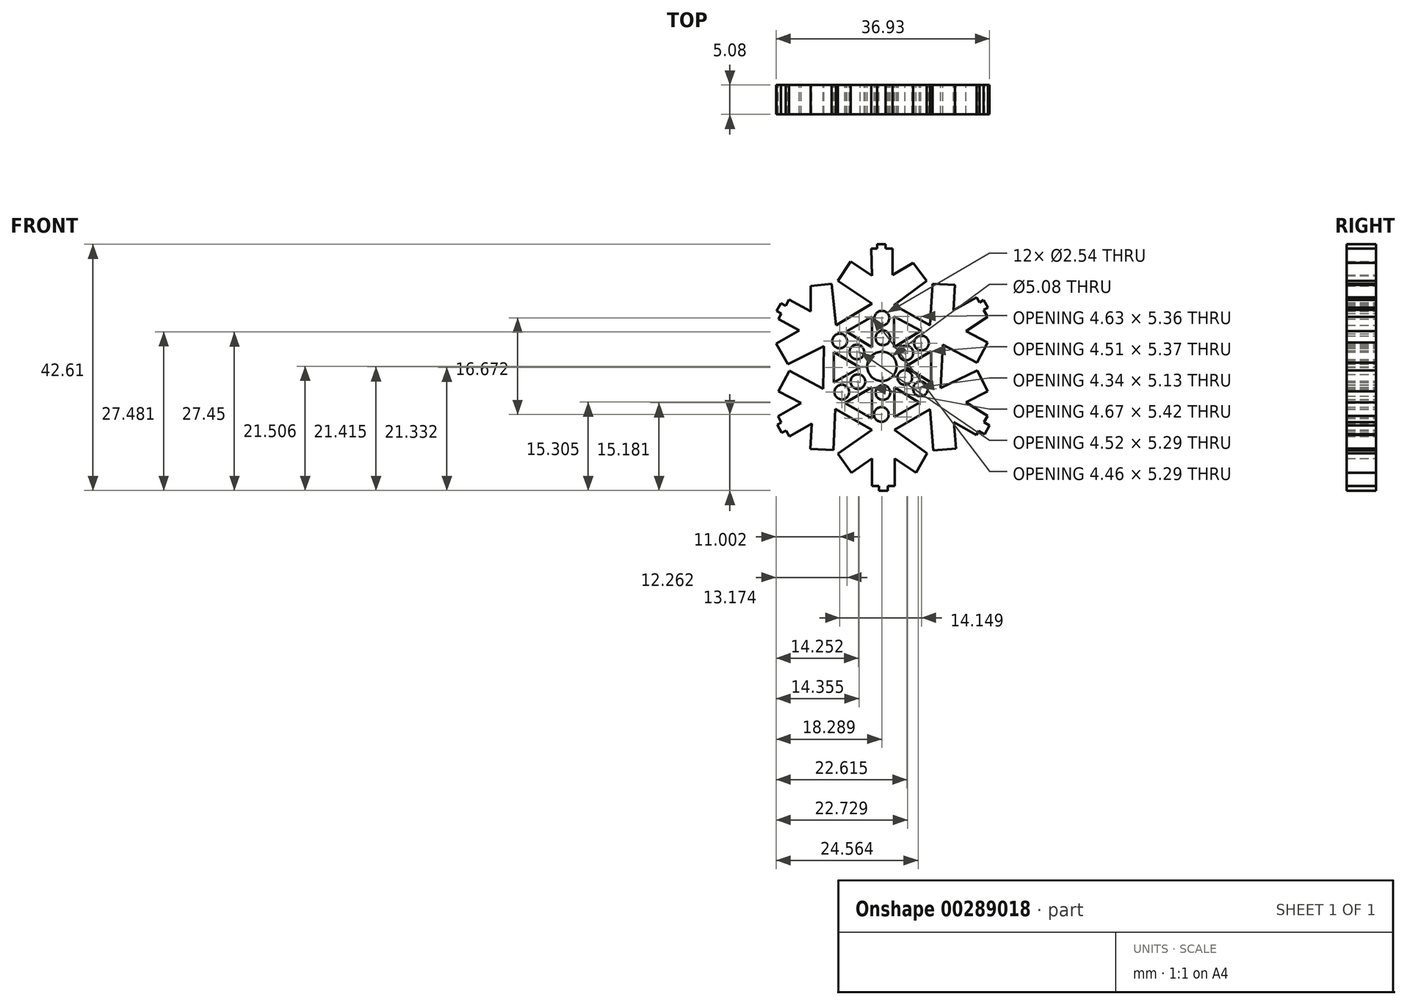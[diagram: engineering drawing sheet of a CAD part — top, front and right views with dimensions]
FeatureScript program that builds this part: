
annotation { "Feature Type Name" : "Feature", "Feature Type Description" : "" }
export const myFeature = defineFeature(function(context is Context, id is Id, definition is map)
    precondition{}
    {
        {
            var Q0;
            Q0=qCreatedBy(makeId("Front.planeOp"),FACE);
            var sketch = newSketch(context, id + "F0", { "sketchPlane" : qUnion([Q0])});
            skLineSegment(sketch, "E0", {"start": v(-24.04, 42.31) * mm, "end": v(-20.36, 42.31) * mm});
            skLineSegment(sketch, "E1", {"start": v(-20.36, 42.31) * mm, "end": v(-20.36, 37.78) * mm});
            skLineSegment(sketch, "E2", {"start": v(-20.36, 37.78) * mm, "end": v(-16.78, 39.86) * mm});
            skLineSegment(sketch, "E3", {"start": v(-16.78, 39.86) * mm, "end": v(-14.46, 36.74) * mm});
            skLineSegment(sketch, "E4", {"start": v(-14.46, 36.74) * mm, "end": v(-20.09, 32.57) * mm});
            skLineSegment(sketch, "E5", {"start": v(-20.09, 32.57) * mm, "end": v(-20.09, 25.26) * mm});
            skLineSegment(sketch, "E6", {"start": v(-20.09, 25.26) * mm, "end": v(-13.89, 29.04) * mm});
            skLineSegment(sketch, "E7", {"start": v(-13.89, 29.04) * mm, "end": v(-13.46, 36.26) * mm});
            skLineSegment(sketch, "E8", {"start": v(-13.46, 36.26) * mm, "end": v(-9.57, 36.03) * mm});
            skLineSegment(sketch, "E9", {"start": v(-9.57, 36.03) * mm, "end": v(-9.83, 31.68) * mm});
            skLineSegment(sketch, "E10", {"start": v(-9.83, 31.68) * mm, "end": v(-5.8, 33.92) * mm});
            skLineSegment(sketch, "E11", {"start": v(-5.8, 33.92) * mm, "end": v(-3.94, 30.55) * mm});
            skLineSegment(sketch, "E12", {"start": v(-3.94, 30.55) * mm, "end": v(-7.67, 28.04) * mm});
            skLineSegment(sketch, "E13", {"start": v(-7.67, 28.04) * mm, "end": v(-3.94, 26.08) * mm});
            skLineSegment(sketch, "E14", {"start": v(-3.94, 26.08) * mm, "end": v(-5.76, 22.61) * mm});
            skLineSegment(sketch, "E15", {"start": v(-5.76, 22.61) * mm, "end": v(-11.69, 25.73) * mm});
            skLineSegment(sketch, "E16", {"start": v(-11.69, 25.73) * mm, "end": v(-18.2, 21.92) * mm});
            skLineSegment(sketch, "E17", {"start": v(-18.2, 21.92) * mm, "end": v(-12.02, 18.19) * mm});
            skLineSegment(sketch, "E18", {"start": v(-12.02, 18.19) * mm, "end": v(-5.67, 21.25) * mm});
            skLineSegment(sketch, "E19", {"start": v(-5.67, 21.25) * mm, "end": v(-3.94, 17.66) * mm});
            skLineSegment(sketch, "E20", {"start": v(-3.94, 17.66) * mm, "end": v(-7.67, 15.75) * mm});
            skLineSegment(sketch, "E21", {"start": v(-7.67, 15.75) * mm, "end": v(-3.94, 13.38) * mm});
            skLineSegment(sketch, "E22", {"start": v(-3.94, 13.38) * mm, "end": v(-5.85, 10.05) * mm});
            skLineSegment(sketch, "E23", {"start": v(-5.85, 10.05) * mm, "end": v(-9.73, 12.28) * mm});
            skLineSegment(sketch, "E24", {"start": v(-9.73, 12.28) * mm, "end": v(-9.37, 7.74) * mm});
            skLineSegment(sketch, "E25", {"start": v(-9.37, 7.74) * mm, "end": v(-13.3, 7.43) * mm});
            skLineSegment(sketch, "E26", {"start": v(-13.3, 7.43) * mm, "end": v(-13.86, 14.5) * mm});
            skLineSegment(sketch, "E27", {"start": v(-13.86, 14.5) * mm, "end": v(-20.03, 18.33) * mm});
            skLineSegment(sketch, "E28", {"start": v(-20.03, 18.33) * mm, "end": v(-20.07, 11) * mm});
            skLineSegment(sketch, "E29", {"start": v(-20.07, 11) * mm, "end": v(-14.36, 6.91) * mm});
            skLineSegment(sketch, "E30", {"start": v(-14.36, 6.91) * mm, "end": v(-16.32, 3.55) * mm});
            skLineSegment(sketch, "E31", {"start": v(-16.32, 3.55) * mm, "end": v(-19.95, 6.04) * mm});
            skLineSegment(sketch, "E32", {"start": v(-19.95, 6.04) * mm, "end": v(-19.95, 1.28) * mm});
            skLineSegment(sketch, "E33", {"start": v(-19.95, 1.28) * mm, "end": v(-23.91, 1.28) * mm});
            skLineSegment(sketch, "E34", {"start": v(-23.91, 1.28) * mm, "end": v(-23.91, 6.03) * mm});
            skLineSegment(sketch, "E35", {"start": v(-23.91, 6.03) * mm, "end": v(-27.5, 3.52) * mm});
            skLineSegment(sketch, "E36", {"start": v(-27.5, 3.52) * mm, "end": v(-29.8, 6.82) * mm});
            skLineSegment(sketch, "E37", {"start": v(-29.8, 6.82) * mm, "end": v(-23.91, 10.95) * mm});
            skLineSegment(sketch, "E38", {"start": v(-23.91, 10.95) * mm, "end": v(-23.91, 18.35) * mm});
            skLineSegment(sketch, "E39", {"start": v(-23.91, 18.35) * mm, "end": v(-30.27, 14.57) * mm});
            skLineSegment(sketch, "E40", {"start": v(-30.27, 14.57) * mm, "end": v(-30.6, 7.47) * mm});
            skLineSegment(sketch, "E41", {"start": v(-30.6, 7.47) * mm, "end": v(-34.56, 7.65) * mm});
            skLineSegment(sketch, "E42", {"start": v(-34.56, 7.65) * mm, "end": v(-34.35, 12.08) * mm});
            skLineSegment(sketch, "E43", {"start": v(-34.35, 12.08) * mm, "end": v(-38.22, 9.85) * mm});
            skLineSegment(sketch, "E44", {"start": v(-38.22, 9.85) * mm, "end": v(-40.2, 13.3) * mm});
            skLineSegment(sketch, "E45", {"start": v(-40.2, 13.3) * mm, "end": v(-36.2, 15.6) * mm});
            skLineSegment(sketch, "E46", {"start": v(-36.2, 15.6) * mm, "end": v(-40.1, 17.65) * mm});
            skLineSegment(sketch, "E47", {"start": v(-40.1, 17.65) * mm, "end": v(-38.22, 21.2) * mm});
            skLineSegment(sketch, "E48", {"start": v(-38.22, 21.2) * mm, "end": v(-32.33, 18.1) * mm});
            skLineSegment(sketch, "E49", {"start": v(-32.33, 18.1) * mm, "end": v(-25.98, 21.75) * mm});
            skLineSegment(sketch, "E50", {"start": v(-25.98, 21.75) * mm, "end": v(-32.25, 25.48) * mm});
            skLineSegment(sketch, "E51", {"start": v(-32.25, 25.48) * mm, "end": v(-38.45, 22.36) * mm});
            skLineSegment(sketch, "E52", {"start": v(-38.45, 22.36) * mm, "end": v(-40.5, 25.9) * mm});
            skLineSegment(sketch, "E53", {"start": v(-40.5, 25.9) * mm, "end": v(-36.51, 28.2) * mm});
            skLineSegment(sketch, "E54", {"start": v(-36.51, 28.2) * mm, "end": v(-40.1, 30.17) * mm});
            skLineSegment(sketch, "E55", {"start": v(-40.1, 30.17) * mm, "end": v(-38.27, 33.5) * mm});
            skLineSegment(sketch, "E56", {"start": v(-38.27, 33.5) * mm, "end": v(-34.55, 31.46) * mm});
            skLineSegment(sketch, "E57", {"start": v(-34.55, 31.46) * mm, "end": v(-34.55, 35.88) * mm});
            skLineSegment(sketch, "E58", {"start": v(-34.55, 35.88) * mm, "end": v(-30.9, 36.26) * mm});
            skLineSegment(sketch, "E59", {"start": v(-30.9, 36.26) * mm, "end": v(-30.15, 29.06) * mm});
            skLineSegment(sketch, "E60", {"start": v(-30.15, 29.06) * mm, "end": v(-23.91, 25.27) * mm});
            skLineSegment(sketch, "E61", {"start": v(-23.91, 25.27) * mm, "end": v(-23.91, 32.81) * mm});
            skLineSegment(sketch, "E62", {"start": v(-23.91, 32.81) * mm, "end": v(-29.81, 36.74) * mm});
            skLineSegment(sketch, "E63", {"start": v(-29.81, 36.74) * mm, "end": v(-27.59, 40.08) * mm});
            skLineSegment(sketch, "E64", {"start": v(-27.59, 40.08) * mm, "end": v(-23.91, 37.64) * mm});
            skLineSegment(sketch, "E65", {"start": v(-23.91, 37.64) * mm, "end": v(-24.04, 42.31) * mm});
            skLineSegment(sketch, "E66", {"start": v(-23, 42.31) * mm, "end": v(-23, 43.07) * mm});
            skLineSegment(sketch, "E67", {"start": v(-23, 43.07) * mm, "end": v(-21.58, 43.07) * mm});
            skLineSegment(sketch, "E68", {"start": v(-21.58, 43.07) * mm, "end": v(-21.58, 42.31) * mm});
            skLineSegment(sketch, "E69", {"start": v(-5.32, 33.03) * mm, "end": v(-4.6, 33.43) * mm});
            skLineSegment(sketch, "E70", {"start": v(-4.6, 33.43) * mm, "end": v(-3.86, 32.12) * mm});
            skLineSegment(sketch, "E71", {"start": v(-3.86, 32.12) * mm, "end": v(-4.59, 31.72) * mm});
            skLineSegment(sketch, "E72", {"start": v(-4.57, 12.29) * mm, "end": v(-3.57, 11.71) * mm});
            skPoint(sketch, "E72.endSnap0", {"position": v(-4.9, 11.71) * mm});
            skLineSegment(sketch, "E73", {"start": v(-3.57, 11.71) * mm, "end": v(-4.42, 10.23) * mm});
            skLineSegment(sketch, "E74", {"start": v(-4.42, 10.23) * mm, "end": v(-5.42, 10.8) * mm});
            skLineSegment(sketch, "E75", {"start": v(-39.59, 31.1) * mm, "end": v(-40.4, 31.55) * mm});
            skLineSegment(sketch, "E76", {"start": v(-40.4, 31.55) * mm, "end": v(-39.66, 32.9) * mm});
            skLineSegment(sketch, "E77", {"start": v(-39.66, 32.9) * mm, "end": v(-38.85, 32.45) * mm});
            skLineSegment(sketch, "E78", {"start": v(-39.6, 12.26) * mm, "end": v(-40.32, 11.84) * mm});
            skLineSegment(sketch, "E79", {"start": v(-40.32, 11.84) * mm, "end": v(-39.51, 10.44) * mm});
            skLineSegment(sketch, "E80", {"start": v(-39.51, 10.44) * mm, "end": v(-38.8, 10.85) * mm});
            skLineSegment(sketch, "E81", {"start": v(-22.7, 1.28) * mm, "end": v(-22.7, 0.46) * mm});
            skLineSegment(sketch, "E82", {"start": v(-22.7, 0.46) * mm, "end": v(-21.18, 0.46) * mm});
            skLineSegment(sketch, "E83", {"start": v(-21.18, 0.46) * mm, "end": v(-21.18, 1.28) * mm});
            skLineSegment(sketch, "E84", {"start": v(-13.89, 29.04) * mm, "end": v(-20.09, 32.57) * mm});
            skLineSegment(sketch, "E85", {"start": v(-20.09, 30.62) * mm, "end": v(-15.45, 28.08) * mm});
            skLineSegment(sketch, "E86", {"start": v(-23.91, 32.81) * mm, "end": v(-30.15, 29.06) * mm});
            skLineSegment(sketch, "E87", {"start": v(-28.38, 27.98) * mm, "end": v(-23.91, 30.55) * mm});
            skLineSegment(sketch, "E88", {"start": v(-23.91, 30.55) * mm, "end": v(-23.91, 32.81) * mm});
            skLineSegment(sketch, "E89", {"start": v(-32.25, 25.48) * mm, "end": v(-32.33, 18.1) * mm});
            skLineSegment(sketch, "E90", {"start": v(-30.5, 19.15) * mm, "end": v(-30.5, 24.44) * mm});
            skLineSegment(sketch, "E91", {"start": v(-30.5, 24.44) * mm, "end": v(-32.25, 25.48) * mm});
            skLineSegment(sketch, "E92", {"start": v(-30.27, 14.57) * mm, "end": v(-23.91, 10.95) * mm});
            skLineSegment(sketch, "E93", {"start": v(-23.91, 12.93) * mm, "end": v(-28.58, 15.58) * mm});
            skLineSegment(sketch, "E94", {"start": v(-28.58, 15.58) * mm, "end": v(-30.27, 14.57) * mm});
            skLineSegment(sketch, "E95", {"start": v(-13.86, 14.5) * mm, "end": v(-20.07, 11) * mm});
            skLineSegment(sketch, "E96", {"start": v(-20.06, 13.2) * mm, "end": v(-15.72, 15.66) * mm});
            skLineSegment(sketch, "E97", {"start": v(-15.72, 15.66) * mm, "end": v(-13.86, 14.5) * mm});
            skLineSegment(sketch, "E98", {"start": v(-11.69, 25.73) * mm, "end": v(-12.02, 18.19) * mm});
            skLineSegment(sketch, "E99", {"start": v(-13.68, 19.19) * mm, "end": v(-13.68, 24.56) * mm});
            skLineSegment(sketch, "E100", {"start": v(-13.68, 24.56) * mm, "end": v(-11.69, 25.73) * mm});
            skSolve(sketch);
        }
        {
            var Q0;
            Q0 = qSketchRegion(id + "F0", true);
            extrude(context, id + "F1", {"entities" : qUnion([Q0]), "depth" : 5.08 * mm});
        }
        {
            var Q0;
            Q0=qCreatedBy(makeId("Front.planeOp"),FACE);
            var sketch = newSketch(context, id + "F2", { "sketchPlane" : qUnion([Q0])});
            skCircle(sketch, "E101", {"center": v(-22.21, 21.97) * mm, "radius": 2.34 * mm});
            skSolve(sketch);
        }
        {
            var Q0;
            Q0=sQuery(id+"F2.wireOp",VERTEX,"E101.center");
            var Q1;
            Q1=makeQuery(id+"F1.opExtrude","SWEPT_BODY",BODY,{"disambiguationData":[OSD([sQuery(id+"F0.wireOp",EDGE,"E0"),sQuery(id+"F0.wireOp",EDGE,"E1"),sQuery(id+"F0.wireOp",EDGE,"E2"),sQuery(id+"F0.wireOp",EDGE,"E3"),sQuery(id+"F0.wireOp",EDGE,"E4"),sQuery(id+"F0.wireOp",EDGE,"E5"),sQuery(id+"F0.wireOp",EDGE,"E6"),sQuery(id+"F0.wireOp",EDGE,"E7"),sQuery(id+"F0.wireOp",EDGE,"E8"),sQuery(id+"F0.wireOp",EDGE,"E9"),sQuery(id+"F0.wireOp",EDGE,"E10"),sQuery(id+"F0.wireOp",EDGE,"E11"),sQuery(id+"F0.wireOp",EDGE,"E12"),sQuery(id+"F0.wireOp",EDGE,"E13"),sQuery(id+"F0.wireOp",EDGE,"E14"),sQuery(id+"F0.wireOp",EDGE,"E15"),sQuery(id+"F0.wireOp",EDGE,"E16"),sQuery(id+"F0.wireOp",EDGE,"E17"),sQuery(id+"F0.wireOp",EDGE,"E18"),sQuery(id+"F0.wireOp",EDGE,"E19"),sQuery(id+"F0.wireOp",EDGE,"E20"),sQuery(id+"F0.wireOp",EDGE,"E21"),sQuery(id+"F0.wireOp",EDGE,"E22"),sQuery(id+"F0.wireOp",EDGE,"E23"),sQuery(id+"F0.wireOp",EDGE,"E24"),sQuery(id+"F0.wireOp",EDGE,"E25"),sQuery(id+"F0.wireOp",EDGE,"E26"),sQuery(id+"F0.wireOp",EDGE,"E27"),sQuery(id+"F0.wireOp",EDGE,"E28"),sQuery(id+"F0.wireOp",EDGE,"E29"),sQuery(id+"F0.wireOp",EDGE,"E30"),sQuery(id+"F0.wireOp",EDGE,"E31"),sQuery(id+"F0.wireOp",EDGE,"E32"),sQuery(id+"F0.wireOp",EDGE,"E33"),sQuery(id+"F0.wireOp",EDGE,"E34"),sQuery(id+"F0.wireOp",EDGE,"E35"),sQuery(id+"F0.wireOp",EDGE,"E36"),sQuery(id+"F0.wireOp",EDGE,"E37"),sQuery(id+"F0.wireOp",EDGE,"E38"),sQuery(id+"F0.wireOp",EDGE,"E39"),sQuery(id+"F0.wireOp",EDGE,"E40"),sQuery(id+"F0.wireOp",EDGE,"E41"),sQuery(id+"F0.wireOp",EDGE,"E42"),sQuery(id+"F0.wireOp",EDGE,"E43"),sQuery(id+"F0.wireOp",EDGE,"E44"),sQuery(id+"F0.wireOp",EDGE,"E45"),sQuery(id+"F0.wireOp",EDGE,"E46"),sQuery(id+"F0.wireOp",EDGE,"E47"),sQuery(id+"F0.wireOp",EDGE,"E48"),sQuery(id+"F0.wireOp",EDGE,"E49"),sQuery(id+"F0.wireOp",EDGE,"E50"),sQuery(id+"F0.wireOp",EDGE,"E51"),sQuery(id+"F0.wireOp",EDGE,"E52"),sQuery(id+"F0.wireOp",EDGE,"E53"),sQuery(id+"F0.wireOp",EDGE,"E54"),sQuery(id+"F0.wireOp",EDGE,"E55"),sQuery(id+"F0.wireOp",EDGE,"E56"),sQuery(id+"F0.wireOp",EDGE,"E57"),sQuery(id+"F0.wireOp",EDGE,"E58"),sQuery(id+"F0.wireOp",EDGE,"E59"),sQuery(id+"F0.wireOp",EDGE,"E60"),sQuery(id+"F0.wireOp",EDGE,"E61"),sQuery(id+"F0.wireOp",EDGE,"E62"),sQuery(id+"F0.wireOp",EDGE,"E63"),sQuery(id+"F0.wireOp",EDGE,"E64"),sQuery(id+"F0.wireOp",EDGE,"E65"),sQuery(id+"F0.wireOp",EDGE,"E66"),sQuery(id+"F0.wireOp",EDGE,"E67"),sQuery(id+"F0.wireOp",EDGE,"E68"),sQuery(id+"F0.wireOp",EDGE,"E69"),sQuery(id+"F0.wireOp",EDGE,"E70"),sQuery(id+"F0.wireOp",EDGE,"E71"),sQuery(id+"F0.wireOp",EDGE,"E72"),sQuery(id+"F0.wireOp",EDGE,"E73"),sQuery(id+"F0.wireOp",EDGE,"E74"),sQuery(id+"F0.wireOp",EDGE,"E75"),sQuery(id+"F0.wireOp",EDGE,"E76"),sQuery(id+"F0.wireOp",EDGE,"E77"),sQuery(id+"F0.wireOp",EDGE,"E78"),sQuery(id+"F0.wireOp",EDGE,"E79"),sQuery(id+"F0.wireOp",EDGE,"E80"),sQuery(id+"F0.wireOp",EDGE,"E81"),sQuery(id+"F0.wireOp",EDGE,"E82"),sQuery(id+"F0.wireOp",EDGE,"E83")])]});
            hole(context, id + "F3", {"style" : HoleStyle.SIMPLE, "endStyle" : HoleEndStyle.THROUGH, "oppositeDirection" : true, "holeDiameter" : 5.08 * mm, "tappedDepth" : 12.7 * mm, "tapClearance" : 3, "locations" : qUnion([Q0]), "scope" : qUnion([Q1])});
        }
        {
            var Q0;
            Q0=qCreatedBy(makeId("Front.planeOp"),FACE);
            var sketch = newSketch(context, id + "F4", { "sketchPlane" : qUnion([Q0])});
            skCircle(sketch, "E102", {"center": v(-22.02, 26.88) * mm, "radius": 1.03 * mm});
            skSolve(sketch);
        }
        {
            var Q0;
            Q0=qCreatedBy(makeId("Front.planeOp"),FACE);
            var sketch = newSketch(context, id + "F5", { "sketchPlane" : qUnion([Q0])});
            skCircle(sketch, "E103", {"center": v(-22.2, 30.3) * mm, "radius": 1.09 * mm});
            skSolve(sketch);
        }
        {
            var Q0;
            Q0=qCreatedBy(makeId("Front.planeOp"),FACE);
            var sketch = newSketch(context, id + "F6", { "sketchPlane" : qUnion([Q0])});
            skCircle(sketch, "E104", {"center": v(-26.52, 24.45) * mm, "radius": 1 * mm});
            skSolve(sketch);
        }
        {
            var Q0;
            Q0=qCreatedBy(makeId("Front.planeOp"),FACE);
            var sketch = newSketch(context, id + "F7", { "sketchPlane" : qUnion([Q0])});
            skCircle(sketch, "E105", {"center": v(-29.5, 26.34) * mm, "radius": 1 * mm});
            skSolve(sketch);
        }
        {
            var Q0;
            Q0=qCreatedBy(makeId("Front.planeOp"),FACE);
            var sketch = newSketch(context, id + "F8", { "sketchPlane" : qUnion([Q0])});
            skCircle(sketch, "E106", {"center": v(-26.34, 19.31) * mm, "radius": 1.02 * mm});
            skSolve(sketch);
        }
        {
            var Q0;
            Q0=qCreatedBy(makeId("Front.planeOp"),FACE);
            var sketch = newSketch(context, id + "F9", { "sketchPlane" : qUnion([Q0])});
            skCircle(sketch, "E107", {"center": v(-29.14, 17.5) * mm, "radius": 0.81 * mm});
            skSolve(sketch);
        }
        {
            var Q0;
            Q0=qCreatedBy(makeId("Front.planeOp"),FACE);
            var sketch = newSketch(context, id + "F10", { "sketchPlane" : qUnion([Q0])});
            skCircle(sketch, "E108", {"center": v(-22.02, 17.42) * mm, "radius": 0.96 * mm});
            skSolve(sketch);
        }
        {
            var Q0;
            Q0=qCreatedBy(makeId("Front.planeOp"),FACE);
            var sketch = newSketch(context, id + "F11", { "sketchPlane" : qUnion([Q0])});
            skCircle(sketch, "E109", {"center": v(-22.29, 13.63) * mm, "radius": 1.09 * mm});
            skSolve(sketch);
        }
        {
            var Q0;
            Q0=qCreatedBy(makeId("Front.planeOp"),FACE);
            var sketch = newSketch(context, id + "F12", { "sketchPlane" : qUnion([Q0])});
            skCircle(sketch, "E110", {"center": v(-18.23, 20.03) * mm, "radius": 1.03 * mm});
            skSolve(sketch);
        }
        {
            var Q0;
            Q0=qCreatedBy(makeId("Front.planeOp"),FACE);
            var sketch = newSketch(context, id + "F13", { "sketchPlane" : qUnion([Q0])});
            skCircle(sketch, "E111", {"center": v(-15.53, 18.05) * mm, "radius": 1.05 * mm});
            skSolve(sketch);
        }
        {
            var Q0;
            Q0=qCreatedBy(makeId("Front.planeOp"),FACE);
            var sketch = newSketch(context, id + "F14", { "sketchPlane" : qUnion([Q0])});
            skCircle(sketch, "E112", {"center": v(-18.05, 24.27) * mm, "radius": 1 * mm});
            skSolve(sketch);
        }
        {
            var Q0;
            Q0=qCreatedBy(makeId("Front.planeOp"),FACE);
            var sketch = newSketch(context, id + "F15", { "sketchPlane" : qUnion([Q0])});
            skCircle(sketch, "E113", {"center": v(-15.35, 25.98) * mm, "radius": 0.96 * mm});
            skSolve(sketch);
        }
        {
            var Q0;
            Q0=sQuery(id+"F5.wireOp",VERTEX,"E103.center");
            var Q1;
            Q1=makeQuery(id+"F1.opExtrude","SWEPT_BODY",BODY,{"disambiguationData":[OSD([sQuery(id+"F0.wireOp",EDGE,"E0"),sQuery(id+"F0.wireOp",EDGE,"E1"),sQuery(id+"F0.wireOp",EDGE,"E2"),sQuery(id+"F0.wireOp",EDGE,"E3"),sQuery(id+"F0.wireOp",EDGE,"E4"),sQuery(id+"F0.wireOp",EDGE,"E5"),sQuery(id+"F0.wireOp",EDGE,"E6"),sQuery(id+"F0.wireOp",EDGE,"E7"),sQuery(id+"F0.wireOp",EDGE,"E8"),sQuery(id+"F0.wireOp",EDGE,"E9"),sQuery(id+"F0.wireOp",EDGE,"E10"),sQuery(id+"F0.wireOp",EDGE,"E11"),sQuery(id+"F0.wireOp",EDGE,"E12"),sQuery(id+"F0.wireOp",EDGE,"E13"),sQuery(id+"F0.wireOp",EDGE,"E14"),sQuery(id+"F0.wireOp",EDGE,"E15"),sQuery(id+"F0.wireOp",EDGE,"E16"),sQuery(id+"F0.wireOp",EDGE,"E17"),sQuery(id+"F0.wireOp",EDGE,"E18"),sQuery(id+"F0.wireOp",EDGE,"E19"),sQuery(id+"F0.wireOp",EDGE,"E20"),sQuery(id+"F0.wireOp",EDGE,"E21"),sQuery(id+"F0.wireOp",EDGE,"E22"),sQuery(id+"F0.wireOp",EDGE,"E23"),sQuery(id+"F0.wireOp",EDGE,"E24"),sQuery(id+"F0.wireOp",EDGE,"E25"),sQuery(id+"F0.wireOp",EDGE,"E26"),sQuery(id+"F0.wireOp",EDGE,"E27"),sQuery(id+"F0.wireOp",EDGE,"E28"),sQuery(id+"F0.wireOp",EDGE,"E29"),sQuery(id+"F0.wireOp",EDGE,"E30"),sQuery(id+"F0.wireOp",EDGE,"E31"),sQuery(id+"F0.wireOp",EDGE,"E32"),sQuery(id+"F0.wireOp",EDGE,"E33"),sQuery(id+"F0.wireOp",EDGE,"E34"),sQuery(id+"F0.wireOp",EDGE,"E35"),sQuery(id+"F0.wireOp",EDGE,"E36"),sQuery(id+"F0.wireOp",EDGE,"E37"),sQuery(id+"F0.wireOp",EDGE,"E38"),sQuery(id+"F0.wireOp",EDGE,"E39"),sQuery(id+"F0.wireOp",EDGE,"E40"),sQuery(id+"F0.wireOp",EDGE,"E41"),sQuery(id+"F0.wireOp",EDGE,"E42"),sQuery(id+"F0.wireOp",EDGE,"E43"),sQuery(id+"F0.wireOp",EDGE,"E44"),sQuery(id+"F0.wireOp",EDGE,"E45"),sQuery(id+"F0.wireOp",EDGE,"E46"),sQuery(id+"F0.wireOp",EDGE,"E47"),sQuery(id+"F0.wireOp",EDGE,"E48"),sQuery(id+"F0.wireOp",EDGE,"E49"),sQuery(id+"F0.wireOp",EDGE,"E50"),sQuery(id+"F0.wireOp",EDGE,"E51"),sQuery(id+"F0.wireOp",EDGE,"E52"),sQuery(id+"F0.wireOp",EDGE,"E53"),sQuery(id+"F0.wireOp",EDGE,"E54"),sQuery(id+"F0.wireOp",EDGE,"E55"),sQuery(id+"F0.wireOp",EDGE,"E56"),sQuery(id+"F0.wireOp",EDGE,"E57"),sQuery(id+"F0.wireOp",EDGE,"E58"),sQuery(id+"F0.wireOp",EDGE,"E59"),sQuery(id+"F0.wireOp",EDGE,"E60"),sQuery(id+"F0.wireOp",EDGE,"E61"),sQuery(id+"F0.wireOp",EDGE,"E62"),sQuery(id+"F0.wireOp",EDGE,"E63"),sQuery(id+"F0.wireOp",EDGE,"E64"),sQuery(id+"F0.wireOp",EDGE,"E65"),sQuery(id+"F0.wireOp",EDGE,"E66"),sQuery(id+"F0.wireOp",EDGE,"E67"),sQuery(id+"F0.wireOp",EDGE,"E68"),sQuery(id+"F0.wireOp",EDGE,"E69"),sQuery(id+"F0.wireOp",EDGE,"E70"),sQuery(id+"F0.wireOp",EDGE,"E71"),sQuery(id+"F0.wireOp",EDGE,"E72"),sQuery(id+"F0.wireOp",EDGE,"E73"),sQuery(id+"F0.wireOp",EDGE,"E74"),sQuery(id+"F0.wireOp",EDGE,"E75"),sQuery(id+"F0.wireOp",EDGE,"E76"),sQuery(id+"F0.wireOp",EDGE,"E77"),sQuery(id+"F0.wireOp",EDGE,"E78"),sQuery(id+"F0.wireOp",EDGE,"E79"),sQuery(id+"F0.wireOp",EDGE,"E80"),sQuery(id+"F0.wireOp",EDGE,"E81"),sQuery(id+"F0.wireOp",EDGE,"E82"),sQuery(id+"F0.wireOp",EDGE,"E83"),sQuery(id+"F0.wireOp",EDGE,"E84"),sQuery(id+"F0.wireOp",EDGE,"E85"),sQuery(id+"F0.wireOp",EDGE,"E86"),sQuery(id+"F0.wireOp",EDGE,"E87"),sQuery(id+"F0.wireOp",EDGE,"E89"),sQuery(id+"F0.wireOp",EDGE,"E90"),sQuery(id+"F0.wireOp",EDGE,"E92"),sQuery(id+"F0.wireOp",EDGE,"E93"),sQuery(id+"F0.wireOp",EDGE,"E95"),sQuery(id+"F0.wireOp",EDGE,"E96"),sQuery(id+"F0.wireOp",EDGE,"E98"),sQuery(id+"F0.wireOp",EDGE,"E99")])]});
            hole(context, id + "F16", {"style" : HoleStyle.SIMPLE, "endStyle" : HoleEndStyle.THROUGH, "oppositeDirection" : true, "holeDiameter" : 2.54 * mm, "tappedDepth" : 12.7 * mm, "tapClearance" : 3, "locations" : qUnion([Q0]), "scope" : qUnion([Q1])});
        }
        {
            var Q0;
            Q0=sQuery(id+"F4.wireOp",VERTEX,"E102.center");
            var Q1;
            Q1=makeQuery(id+"F1.opExtrude","SWEPT_BODY",BODY,{"disambiguationData":[OSD([sQuery(id+"F0.wireOp",EDGE,"E0"),sQuery(id+"F0.wireOp",EDGE,"E1"),sQuery(id+"F0.wireOp",EDGE,"E2"),sQuery(id+"F0.wireOp",EDGE,"E3"),sQuery(id+"F0.wireOp",EDGE,"E4"),sQuery(id+"F0.wireOp",EDGE,"E5"),sQuery(id+"F0.wireOp",EDGE,"E6"),sQuery(id+"F0.wireOp",EDGE,"E7"),sQuery(id+"F0.wireOp",EDGE,"E8"),sQuery(id+"F0.wireOp",EDGE,"E9"),sQuery(id+"F0.wireOp",EDGE,"E10"),sQuery(id+"F0.wireOp",EDGE,"E11"),sQuery(id+"F0.wireOp",EDGE,"E12"),sQuery(id+"F0.wireOp",EDGE,"E13"),sQuery(id+"F0.wireOp",EDGE,"E14"),sQuery(id+"F0.wireOp",EDGE,"E15"),sQuery(id+"F0.wireOp",EDGE,"E16"),sQuery(id+"F0.wireOp",EDGE,"E17"),sQuery(id+"F0.wireOp",EDGE,"E18"),sQuery(id+"F0.wireOp",EDGE,"E19"),sQuery(id+"F0.wireOp",EDGE,"E20"),sQuery(id+"F0.wireOp",EDGE,"E21"),sQuery(id+"F0.wireOp",EDGE,"E22"),sQuery(id+"F0.wireOp",EDGE,"E23"),sQuery(id+"F0.wireOp",EDGE,"E24"),sQuery(id+"F0.wireOp",EDGE,"E25"),sQuery(id+"F0.wireOp",EDGE,"E26"),sQuery(id+"F0.wireOp",EDGE,"E27"),sQuery(id+"F0.wireOp",EDGE,"E28"),sQuery(id+"F0.wireOp",EDGE,"E29"),sQuery(id+"F0.wireOp",EDGE,"E30"),sQuery(id+"F0.wireOp",EDGE,"E31"),sQuery(id+"F0.wireOp",EDGE,"E32"),sQuery(id+"F0.wireOp",EDGE,"E33"),sQuery(id+"F0.wireOp",EDGE,"E34"),sQuery(id+"F0.wireOp",EDGE,"E35"),sQuery(id+"F0.wireOp",EDGE,"E36"),sQuery(id+"F0.wireOp",EDGE,"E37"),sQuery(id+"F0.wireOp",EDGE,"E38"),sQuery(id+"F0.wireOp",EDGE,"E39"),sQuery(id+"F0.wireOp",EDGE,"E40"),sQuery(id+"F0.wireOp",EDGE,"E41"),sQuery(id+"F0.wireOp",EDGE,"E42"),sQuery(id+"F0.wireOp",EDGE,"E43"),sQuery(id+"F0.wireOp",EDGE,"E44"),sQuery(id+"F0.wireOp",EDGE,"E45"),sQuery(id+"F0.wireOp",EDGE,"E46"),sQuery(id+"F0.wireOp",EDGE,"E47"),sQuery(id+"F0.wireOp",EDGE,"E48"),sQuery(id+"F0.wireOp",EDGE,"E49"),sQuery(id+"F0.wireOp",EDGE,"E50"),sQuery(id+"F0.wireOp",EDGE,"E51"),sQuery(id+"F0.wireOp",EDGE,"E52"),sQuery(id+"F0.wireOp",EDGE,"E53"),sQuery(id+"F0.wireOp",EDGE,"E54"),sQuery(id+"F0.wireOp",EDGE,"E55"),sQuery(id+"F0.wireOp",EDGE,"E56"),sQuery(id+"F0.wireOp",EDGE,"E57"),sQuery(id+"F0.wireOp",EDGE,"E58"),sQuery(id+"F0.wireOp",EDGE,"E59"),sQuery(id+"F0.wireOp",EDGE,"E60"),sQuery(id+"F0.wireOp",EDGE,"E61"),sQuery(id+"F0.wireOp",EDGE,"E62"),sQuery(id+"F0.wireOp",EDGE,"E63"),sQuery(id+"F0.wireOp",EDGE,"E64"),sQuery(id+"F0.wireOp",EDGE,"E65"),sQuery(id+"F0.wireOp",EDGE,"E66"),sQuery(id+"F0.wireOp",EDGE,"E67"),sQuery(id+"F0.wireOp",EDGE,"E68"),sQuery(id+"F0.wireOp",EDGE,"E69"),sQuery(id+"F0.wireOp",EDGE,"E70"),sQuery(id+"F0.wireOp",EDGE,"E71"),sQuery(id+"F0.wireOp",EDGE,"E72"),sQuery(id+"F0.wireOp",EDGE,"E73"),sQuery(id+"F0.wireOp",EDGE,"E74"),sQuery(id+"F0.wireOp",EDGE,"E75"),sQuery(id+"F0.wireOp",EDGE,"E76"),sQuery(id+"F0.wireOp",EDGE,"E77"),sQuery(id+"F0.wireOp",EDGE,"E78"),sQuery(id+"F0.wireOp",EDGE,"E79"),sQuery(id+"F0.wireOp",EDGE,"E80"),sQuery(id+"F0.wireOp",EDGE,"E81"),sQuery(id+"F0.wireOp",EDGE,"E82"),sQuery(id+"F0.wireOp",EDGE,"E83"),sQuery(id+"F0.wireOp",EDGE,"E84"),sQuery(id+"F0.wireOp",EDGE,"E85"),sQuery(id+"F0.wireOp",EDGE,"E86"),sQuery(id+"F0.wireOp",EDGE,"E87"),sQuery(id+"F0.wireOp",EDGE,"E89"),sQuery(id+"F0.wireOp",EDGE,"E90"),sQuery(id+"F0.wireOp",EDGE,"E92"),sQuery(id+"F0.wireOp",EDGE,"E93"),sQuery(id+"F0.wireOp",EDGE,"E95"),sQuery(id+"F0.wireOp",EDGE,"E96"),sQuery(id+"F0.wireOp",EDGE,"E98"),sQuery(id+"F0.wireOp",EDGE,"E99")])]});
            hole(context, id + "F17", {"style" : HoleStyle.SIMPLE, "endStyle" : HoleEndStyle.THROUGH, "oppositeDirection" : true, "holeDiameter" : 2.54 * mm, "tappedDepth" : 12.7 * mm, "tapClearance" : 3, "locations" : qUnion([Q0]), "scope" : qUnion([Q1])});
        }
        {
            var Q0;
            Q0=sQuery(id+"F14.wireOp",VERTEX,"E112.center");
            var Q1;
            Q1=makeQuery(id+"F1.opExtrude","SWEPT_BODY",BODY,{"disambiguationData":[OSD([sQuery(id+"F0.wireOp",EDGE,"E0"),sQuery(id+"F0.wireOp",EDGE,"E1"),sQuery(id+"F0.wireOp",EDGE,"E2"),sQuery(id+"F0.wireOp",EDGE,"E3"),sQuery(id+"F0.wireOp",EDGE,"E4"),sQuery(id+"F0.wireOp",EDGE,"E5"),sQuery(id+"F0.wireOp",EDGE,"E6"),sQuery(id+"F0.wireOp",EDGE,"E7"),sQuery(id+"F0.wireOp",EDGE,"E8"),sQuery(id+"F0.wireOp",EDGE,"E9"),sQuery(id+"F0.wireOp",EDGE,"E10"),sQuery(id+"F0.wireOp",EDGE,"E11"),sQuery(id+"F0.wireOp",EDGE,"E12"),sQuery(id+"F0.wireOp",EDGE,"E13"),sQuery(id+"F0.wireOp",EDGE,"E14"),sQuery(id+"F0.wireOp",EDGE,"E15"),sQuery(id+"F0.wireOp",EDGE,"E16"),sQuery(id+"F0.wireOp",EDGE,"E17"),sQuery(id+"F0.wireOp",EDGE,"E18"),sQuery(id+"F0.wireOp",EDGE,"E19"),sQuery(id+"F0.wireOp",EDGE,"E20"),sQuery(id+"F0.wireOp",EDGE,"E21"),sQuery(id+"F0.wireOp",EDGE,"E22"),sQuery(id+"F0.wireOp",EDGE,"E23"),sQuery(id+"F0.wireOp",EDGE,"E24"),sQuery(id+"F0.wireOp",EDGE,"E25"),sQuery(id+"F0.wireOp",EDGE,"E26"),sQuery(id+"F0.wireOp",EDGE,"E27"),sQuery(id+"F0.wireOp",EDGE,"E28"),sQuery(id+"F0.wireOp",EDGE,"E29"),sQuery(id+"F0.wireOp",EDGE,"E30"),sQuery(id+"F0.wireOp",EDGE,"E31"),sQuery(id+"F0.wireOp",EDGE,"E32"),sQuery(id+"F0.wireOp",EDGE,"E33"),sQuery(id+"F0.wireOp",EDGE,"E34"),sQuery(id+"F0.wireOp",EDGE,"E35"),sQuery(id+"F0.wireOp",EDGE,"E36"),sQuery(id+"F0.wireOp",EDGE,"E37"),sQuery(id+"F0.wireOp",EDGE,"E38"),sQuery(id+"F0.wireOp",EDGE,"E39"),sQuery(id+"F0.wireOp",EDGE,"E40"),sQuery(id+"F0.wireOp",EDGE,"E41"),sQuery(id+"F0.wireOp",EDGE,"E42"),sQuery(id+"F0.wireOp",EDGE,"E43"),sQuery(id+"F0.wireOp",EDGE,"E44"),sQuery(id+"F0.wireOp",EDGE,"E45"),sQuery(id+"F0.wireOp",EDGE,"E46"),sQuery(id+"F0.wireOp",EDGE,"E47"),sQuery(id+"F0.wireOp",EDGE,"E48"),sQuery(id+"F0.wireOp",EDGE,"E49"),sQuery(id+"F0.wireOp",EDGE,"E50"),sQuery(id+"F0.wireOp",EDGE,"E51"),sQuery(id+"F0.wireOp",EDGE,"E52"),sQuery(id+"F0.wireOp",EDGE,"E53"),sQuery(id+"F0.wireOp",EDGE,"E54"),sQuery(id+"F0.wireOp",EDGE,"E55"),sQuery(id+"F0.wireOp",EDGE,"E56"),sQuery(id+"F0.wireOp",EDGE,"E57"),sQuery(id+"F0.wireOp",EDGE,"E58"),sQuery(id+"F0.wireOp",EDGE,"E59"),sQuery(id+"F0.wireOp",EDGE,"E60"),sQuery(id+"F0.wireOp",EDGE,"E61"),sQuery(id+"F0.wireOp",EDGE,"E62"),sQuery(id+"F0.wireOp",EDGE,"E63"),sQuery(id+"F0.wireOp",EDGE,"E64"),sQuery(id+"F0.wireOp",EDGE,"E65"),sQuery(id+"F0.wireOp",EDGE,"E66"),sQuery(id+"F0.wireOp",EDGE,"E67"),sQuery(id+"F0.wireOp",EDGE,"E68"),sQuery(id+"F0.wireOp",EDGE,"E69"),sQuery(id+"F0.wireOp",EDGE,"E70"),sQuery(id+"F0.wireOp",EDGE,"E71"),sQuery(id+"F0.wireOp",EDGE,"E72"),sQuery(id+"F0.wireOp",EDGE,"E73"),sQuery(id+"F0.wireOp",EDGE,"E74"),sQuery(id+"F0.wireOp",EDGE,"E75"),sQuery(id+"F0.wireOp",EDGE,"E76"),sQuery(id+"F0.wireOp",EDGE,"E77"),sQuery(id+"F0.wireOp",EDGE,"E78"),sQuery(id+"F0.wireOp",EDGE,"E79"),sQuery(id+"F0.wireOp",EDGE,"E80"),sQuery(id+"F0.wireOp",EDGE,"E81"),sQuery(id+"F0.wireOp",EDGE,"E82"),sQuery(id+"F0.wireOp",EDGE,"E83"),sQuery(id+"F0.wireOp",EDGE,"E84"),sQuery(id+"F0.wireOp",EDGE,"E85"),sQuery(id+"F0.wireOp",EDGE,"E86"),sQuery(id+"F0.wireOp",EDGE,"E87"),sQuery(id+"F0.wireOp",EDGE,"E89"),sQuery(id+"F0.wireOp",EDGE,"E90"),sQuery(id+"F0.wireOp",EDGE,"E92"),sQuery(id+"F0.wireOp",EDGE,"E93"),sQuery(id+"F0.wireOp",EDGE,"E95"),sQuery(id+"F0.wireOp",EDGE,"E96"),sQuery(id+"F0.wireOp",EDGE,"E98"),sQuery(id+"F0.wireOp",EDGE,"E99")])]});
            hole(context, id + "F18", {"style" : HoleStyle.SIMPLE, "endStyle" : HoleEndStyle.THROUGH, "oppositeDirection" : true, "holeDiameter" : 2.54 * mm, "tappedDepth" : 12.7 * mm, "tapClearance" : 3, "locations" : qUnion([Q0]), "scope" : qUnion([Q1])});
        }
        {
            var Q0;
            Q0=sQuery(id+"F15.wireOp",VERTEX,"E113.center");
            var Q1;
            Q1=makeQuery(id+"F1.opExtrude","SWEPT_BODY",BODY,{"disambiguationData":[OSD([sQuery(id+"F0.wireOp",EDGE,"E0"),sQuery(id+"F0.wireOp",EDGE,"E1"),sQuery(id+"F0.wireOp",EDGE,"E2"),sQuery(id+"F0.wireOp",EDGE,"E3"),sQuery(id+"F0.wireOp",EDGE,"E4"),sQuery(id+"F0.wireOp",EDGE,"E5"),sQuery(id+"F0.wireOp",EDGE,"E6"),sQuery(id+"F0.wireOp",EDGE,"E7"),sQuery(id+"F0.wireOp",EDGE,"E8"),sQuery(id+"F0.wireOp",EDGE,"E9"),sQuery(id+"F0.wireOp",EDGE,"E10"),sQuery(id+"F0.wireOp",EDGE,"E11"),sQuery(id+"F0.wireOp",EDGE,"E12"),sQuery(id+"F0.wireOp",EDGE,"E13"),sQuery(id+"F0.wireOp",EDGE,"E14"),sQuery(id+"F0.wireOp",EDGE,"E15"),sQuery(id+"F0.wireOp",EDGE,"E16"),sQuery(id+"F0.wireOp",EDGE,"E17"),sQuery(id+"F0.wireOp",EDGE,"E18"),sQuery(id+"F0.wireOp",EDGE,"E19"),sQuery(id+"F0.wireOp",EDGE,"E20"),sQuery(id+"F0.wireOp",EDGE,"E21"),sQuery(id+"F0.wireOp",EDGE,"E22"),sQuery(id+"F0.wireOp",EDGE,"E23"),sQuery(id+"F0.wireOp",EDGE,"E24"),sQuery(id+"F0.wireOp",EDGE,"E25"),sQuery(id+"F0.wireOp",EDGE,"E26"),sQuery(id+"F0.wireOp",EDGE,"E27"),sQuery(id+"F0.wireOp",EDGE,"E28"),sQuery(id+"F0.wireOp",EDGE,"E29"),sQuery(id+"F0.wireOp",EDGE,"E30"),sQuery(id+"F0.wireOp",EDGE,"E31"),sQuery(id+"F0.wireOp",EDGE,"E32"),sQuery(id+"F0.wireOp",EDGE,"E33"),sQuery(id+"F0.wireOp",EDGE,"E34"),sQuery(id+"F0.wireOp",EDGE,"E35"),sQuery(id+"F0.wireOp",EDGE,"E36"),sQuery(id+"F0.wireOp",EDGE,"E37"),sQuery(id+"F0.wireOp",EDGE,"E38"),sQuery(id+"F0.wireOp",EDGE,"E39"),sQuery(id+"F0.wireOp",EDGE,"E40"),sQuery(id+"F0.wireOp",EDGE,"E41"),sQuery(id+"F0.wireOp",EDGE,"E42"),sQuery(id+"F0.wireOp",EDGE,"E43"),sQuery(id+"F0.wireOp",EDGE,"E44"),sQuery(id+"F0.wireOp",EDGE,"E45"),sQuery(id+"F0.wireOp",EDGE,"E46"),sQuery(id+"F0.wireOp",EDGE,"E47"),sQuery(id+"F0.wireOp",EDGE,"E48"),sQuery(id+"F0.wireOp",EDGE,"E49"),sQuery(id+"F0.wireOp",EDGE,"E50"),sQuery(id+"F0.wireOp",EDGE,"E51"),sQuery(id+"F0.wireOp",EDGE,"E52"),sQuery(id+"F0.wireOp",EDGE,"E53"),sQuery(id+"F0.wireOp",EDGE,"E54"),sQuery(id+"F0.wireOp",EDGE,"E55"),sQuery(id+"F0.wireOp",EDGE,"E56"),sQuery(id+"F0.wireOp",EDGE,"E57"),sQuery(id+"F0.wireOp",EDGE,"E58"),sQuery(id+"F0.wireOp",EDGE,"E59"),sQuery(id+"F0.wireOp",EDGE,"E60"),sQuery(id+"F0.wireOp",EDGE,"E61"),sQuery(id+"F0.wireOp",EDGE,"E62"),sQuery(id+"F0.wireOp",EDGE,"E63"),sQuery(id+"F0.wireOp",EDGE,"E64"),sQuery(id+"F0.wireOp",EDGE,"E65"),sQuery(id+"F0.wireOp",EDGE,"E66"),sQuery(id+"F0.wireOp",EDGE,"E67"),sQuery(id+"F0.wireOp",EDGE,"E68"),sQuery(id+"F0.wireOp",EDGE,"E69"),sQuery(id+"F0.wireOp",EDGE,"E70"),sQuery(id+"F0.wireOp",EDGE,"E71"),sQuery(id+"F0.wireOp",EDGE,"E72"),sQuery(id+"F0.wireOp",EDGE,"E73"),sQuery(id+"F0.wireOp",EDGE,"E74"),sQuery(id+"F0.wireOp",EDGE,"E75"),sQuery(id+"F0.wireOp",EDGE,"E76"),sQuery(id+"F0.wireOp",EDGE,"E77"),sQuery(id+"F0.wireOp",EDGE,"E78"),sQuery(id+"F0.wireOp",EDGE,"E79"),sQuery(id+"F0.wireOp",EDGE,"E80"),sQuery(id+"F0.wireOp",EDGE,"E81"),sQuery(id+"F0.wireOp",EDGE,"E82"),sQuery(id+"F0.wireOp",EDGE,"E83"),sQuery(id+"F0.wireOp",EDGE,"E84"),sQuery(id+"F0.wireOp",EDGE,"E85"),sQuery(id+"F0.wireOp",EDGE,"E86"),sQuery(id+"F0.wireOp",EDGE,"E87"),sQuery(id+"F0.wireOp",EDGE,"E89"),sQuery(id+"F0.wireOp",EDGE,"E90"),sQuery(id+"F0.wireOp",EDGE,"E92"),sQuery(id+"F0.wireOp",EDGE,"E93"),sQuery(id+"F0.wireOp",EDGE,"E95"),sQuery(id+"F0.wireOp",EDGE,"E96"),sQuery(id+"F0.wireOp",EDGE,"E98"),sQuery(id+"F0.wireOp",EDGE,"E99")])]});
            hole(context, id + "F19", {"style" : HoleStyle.SIMPLE, "endStyle" : HoleEndStyle.THROUGH, "oppositeDirection" : true, "holeDiameter" : 2.54 * mm, "tappedDepth" : 12.7 * mm, "tapClearance" : 3, "locations" : qUnion([Q0]), "scope" : qUnion([Q1])});
        }
        {
            var Q0;
            Q0=sQuery(id+"F12.wireOp",VERTEX,"E110.center");
            var Q1;
            Q1=makeQuery(id+"F1.opExtrude","SWEPT_BODY",BODY,{"disambiguationData":[OSD([sQuery(id+"F0.wireOp",EDGE,"E0"),sQuery(id+"F0.wireOp",EDGE,"E1"),sQuery(id+"F0.wireOp",EDGE,"E2"),sQuery(id+"F0.wireOp",EDGE,"E3"),sQuery(id+"F0.wireOp",EDGE,"E4"),sQuery(id+"F0.wireOp",EDGE,"E5"),sQuery(id+"F0.wireOp",EDGE,"E6"),sQuery(id+"F0.wireOp",EDGE,"E7"),sQuery(id+"F0.wireOp",EDGE,"E8"),sQuery(id+"F0.wireOp",EDGE,"E9"),sQuery(id+"F0.wireOp",EDGE,"E10"),sQuery(id+"F0.wireOp",EDGE,"E11"),sQuery(id+"F0.wireOp",EDGE,"E12"),sQuery(id+"F0.wireOp",EDGE,"E13"),sQuery(id+"F0.wireOp",EDGE,"E14"),sQuery(id+"F0.wireOp",EDGE,"E15"),sQuery(id+"F0.wireOp",EDGE,"E16"),sQuery(id+"F0.wireOp",EDGE,"E17"),sQuery(id+"F0.wireOp",EDGE,"E18"),sQuery(id+"F0.wireOp",EDGE,"E19"),sQuery(id+"F0.wireOp",EDGE,"E20"),sQuery(id+"F0.wireOp",EDGE,"E21"),sQuery(id+"F0.wireOp",EDGE,"E22"),sQuery(id+"F0.wireOp",EDGE,"E23"),sQuery(id+"F0.wireOp",EDGE,"E24"),sQuery(id+"F0.wireOp",EDGE,"E25"),sQuery(id+"F0.wireOp",EDGE,"E26"),sQuery(id+"F0.wireOp",EDGE,"E27"),sQuery(id+"F0.wireOp",EDGE,"E28"),sQuery(id+"F0.wireOp",EDGE,"E29"),sQuery(id+"F0.wireOp",EDGE,"E30"),sQuery(id+"F0.wireOp",EDGE,"E31"),sQuery(id+"F0.wireOp",EDGE,"E32"),sQuery(id+"F0.wireOp",EDGE,"E33"),sQuery(id+"F0.wireOp",EDGE,"E34"),sQuery(id+"F0.wireOp",EDGE,"E35"),sQuery(id+"F0.wireOp",EDGE,"E36"),sQuery(id+"F0.wireOp",EDGE,"E37"),sQuery(id+"F0.wireOp",EDGE,"E38"),sQuery(id+"F0.wireOp",EDGE,"E39"),sQuery(id+"F0.wireOp",EDGE,"E40"),sQuery(id+"F0.wireOp",EDGE,"E41"),sQuery(id+"F0.wireOp",EDGE,"E42"),sQuery(id+"F0.wireOp",EDGE,"E43"),sQuery(id+"F0.wireOp",EDGE,"E44"),sQuery(id+"F0.wireOp",EDGE,"E45"),sQuery(id+"F0.wireOp",EDGE,"E46"),sQuery(id+"F0.wireOp",EDGE,"E47"),sQuery(id+"F0.wireOp",EDGE,"E48"),sQuery(id+"F0.wireOp",EDGE,"E49"),sQuery(id+"F0.wireOp",EDGE,"E50"),sQuery(id+"F0.wireOp",EDGE,"E51"),sQuery(id+"F0.wireOp",EDGE,"E52"),sQuery(id+"F0.wireOp",EDGE,"E53"),sQuery(id+"F0.wireOp",EDGE,"E54"),sQuery(id+"F0.wireOp",EDGE,"E55"),sQuery(id+"F0.wireOp",EDGE,"E56"),sQuery(id+"F0.wireOp",EDGE,"E57"),sQuery(id+"F0.wireOp",EDGE,"E58"),sQuery(id+"F0.wireOp",EDGE,"E59"),sQuery(id+"F0.wireOp",EDGE,"E60"),sQuery(id+"F0.wireOp",EDGE,"E61"),sQuery(id+"F0.wireOp",EDGE,"E62"),sQuery(id+"F0.wireOp",EDGE,"E63"),sQuery(id+"F0.wireOp",EDGE,"E64"),sQuery(id+"F0.wireOp",EDGE,"E65"),sQuery(id+"F0.wireOp",EDGE,"E66"),sQuery(id+"F0.wireOp",EDGE,"E67"),sQuery(id+"F0.wireOp",EDGE,"E68"),sQuery(id+"F0.wireOp",EDGE,"E69"),sQuery(id+"F0.wireOp",EDGE,"E70"),sQuery(id+"F0.wireOp",EDGE,"E71"),sQuery(id+"F0.wireOp",EDGE,"E72"),sQuery(id+"F0.wireOp",EDGE,"E73"),sQuery(id+"F0.wireOp",EDGE,"E74"),sQuery(id+"F0.wireOp",EDGE,"E75"),sQuery(id+"F0.wireOp",EDGE,"E76"),sQuery(id+"F0.wireOp",EDGE,"E77"),sQuery(id+"F0.wireOp",EDGE,"E78"),sQuery(id+"F0.wireOp",EDGE,"E79"),sQuery(id+"F0.wireOp",EDGE,"E80"),sQuery(id+"F0.wireOp",EDGE,"E81"),sQuery(id+"F0.wireOp",EDGE,"E82"),sQuery(id+"F0.wireOp",EDGE,"E83"),sQuery(id+"F0.wireOp",EDGE,"E84"),sQuery(id+"F0.wireOp",EDGE,"E85"),sQuery(id+"F0.wireOp",EDGE,"E86"),sQuery(id+"F0.wireOp",EDGE,"E87"),sQuery(id+"F0.wireOp",EDGE,"E89"),sQuery(id+"F0.wireOp",EDGE,"E90"),sQuery(id+"F0.wireOp",EDGE,"E92"),sQuery(id+"F0.wireOp",EDGE,"E93"),sQuery(id+"F0.wireOp",EDGE,"E95"),sQuery(id+"F0.wireOp",EDGE,"E96"),sQuery(id+"F0.wireOp",EDGE,"E98"),sQuery(id+"F0.wireOp",EDGE,"E99")])]});
            hole(context, id + "F20", {"style" : HoleStyle.SIMPLE, "endStyle" : HoleEndStyle.THROUGH, "oppositeDirection" : true, "holeDiameter" : 2.54 * mm, "tappedDepth" : 12.7 * mm, "tapClearance" : 3, "locations" : qUnion([Q0]), "scope" : qUnion([Q1])});
        }
        {
            var Q0;
            Q0=sQuery(id+"F13.wireOp",VERTEX,"E111.center");
            var Q1;
            Q1=makeQuery(id+"F1.opExtrude","SWEPT_BODY",BODY,{"disambiguationData":[OSD([sQuery(id+"F0.wireOp",EDGE,"E0"),sQuery(id+"F0.wireOp",EDGE,"E1"),sQuery(id+"F0.wireOp",EDGE,"E2"),sQuery(id+"F0.wireOp",EDGE,"E3"),sQuery(id+"F0.wireOp",EDGE,"E4"),sQuery(id+"F0.wireOp",EDGE,"E5"),sQuery(id+"F0.wireOp",EDGE,"E6"),sQuery(id+"F0.wireOp",EDGE,"E7"),sQuery(id+"F0.wireOp",EDGE,"E8"),sQuery(id+"F0.wireOp",EDGE,"E9"),sQuery(id+"F0.wireOp",EDGE,"E10"),sQuery(id+"F0.wireOp",EDGE,"E11"),sQuery(id+"F0.wireOp",EDGE,"E12"),sQuery(id+"F0.wireOp",EDGE,"E13"),sQuery(id+"F0.wireOp",EDGE,"E14"),sQuery(id+"F0.wireOp",EDGE,"E15"),sQuery(id+"F0.wireOp",EDGE,"E16"),sQuery(id+"F0.wireOp",EDGE,"E17"),sQuery(id+"F0.wireOp",EDGE,"E18"),sQuery(id+"F0.wireOp",EDGE,"E19"),sQuery(id+"F0.wireOp",EDGE,"E20"),sQuery(id+"F0.wireOp",EDGE,"E21"),sQuery(id+"F0.wireOp",EDGE,"E22"),sQuery(id+"F0.wireOp",EDGE,"E23"),sQuery(id+"F0.wireOp",EDGE,"E24"),sQuery(id+"F0.wireOp",EDGE,"E25"),sQuery(id+"F0.wireOp",EDGE,"E26"),sQuery(id+"F0.wireOp",EDGE,"E27"),sQuery(id+"F0.wireOp",EDGE,"E28"),sQuery(id+"F0.wireOp",EDGE,"E29"),sQuery(id+"F0.wireOp",EDGE,"E30"),sQuery(id+"F0.wireOp",EDGE,"E31"),sQuery(id+"F0.wireOp",EDGE,"E32"),sQuery(id+"F0.wireOp",EDGE,"E33"),sQuery(id+"F0.wireOp",EDGE,"E34"),sQuery(id+"F0.wireOp",EDGE,"E35"),sQuery(id+"F0.wireOp",EDGE,"E36"),sQuery(id+"F0.wireOp",EDGE,"E37"),sQuery(id+"F0.wireOp",EDGE,"E38"),sQuery(id+"F0.wireOp",EDGE,"E39"),sQuery(id+"F0.wireOp",EDGE,"E40"),sQuery(id+"F0.wireOp",EDGE,"E41"),sQuery(id+"F0.wireOp",EDGE,"E42"),sQuery(id+"F0.wireOp",EDGE,"E43"),sQuery(id+"F0.wireOp",EDGE,"E44"),sQuery(id+"F0.wireOp",EDGE,"E45"),sQuery(id+"F0.wireOp",EDGE,"E46"),sQuery(id+"F0.wireOp",EDGE,"E47"),sQuery(id+"F0.wireOp",EDGE,"E48"),sQuery(id+"F0.wireOp",EDGE,"E49"),sQuery(id+"F0.wireOp",EDGE,"E50"),sQuery(id+"F0.wireOp",EDGE,"E51"),sQuery(id+"F0.wireOp",EDGE,"E52"),sQuery(id+"F0.wireOp",EDGE,"E53"),sQuery(id+"F0.wireOp",EDGE,"E54"),sQuery(id+"F0.wireOp",EDGE,"E55"),sQuery(id+"F0.wireOp",EDGE,"E56"),sQuery(id+"F0.wireOp",EDGE,"E57"),sQuery(id+"F0.wireOp",EDGE,"E58"),sQuery(id+"F0.wireOp",EDGE,"E59"),sQuery(id+"F0.wireOp",EDGE,"E60"),sQuery(id+"F0.wireOp",EDGE,"E61"),sQuery(id+"F0.wireOp",EDGE,"E62"),sQuery(id+"F0.wireOp",EDGE,"E63"),sQuery(id+"F0.wireOp",EDGE,"E64"),sQuery(id+"F0.wireOp",EDGE,"E65"),sQuery(id+"F0.wireOp",EDGE,"E66"),sQuery(id+"F0.wireOp",EDGE,"E67"),sQuery(id+"F0.wireOp",EDGE,"E68"),sQuery(id+"F0.wireOp",EDGE,"E69"),sQuery(id+"F0.wireOp",EDGE,"E70"),sQuery(id+"F0.wireOp",EDGE,"E71"),sQuery(id+"F0.wireOp",EDGE,"E72"),sQuery(id+"F0.wireOp",EDGE,"E73"),sQuery(id+"F0.wireOp",EDGE,"E74"),sQuery(id+"F0.wireOp",EDGE,"E75"),sQuery(id+"F0.wireOp",EDGE,"E76"),sQuery(id+"F0.wireOp",EDGE,"E77"),sQuery(id+"F0.wireOp",EDGE,"E78"),sQuery(id+"F0.wireOp",EDGE,"E79"),sQuery(id+"F0.wireOp",EDGE,"E80"),sQuery(id+"F0.wireOp",EDGE,"E81"),sQuery(id+"F0.wireOp",EDGE,"E82"),sQuery(id+"F0.wireOp",EDGE,"E83"),sQuery(id+"F0.wireOp",EDGE,"E84"),sQuery(id+"F0.wireOp",EDGE,"E85"),sQuery(id+"F0.wireOp",EDGE,"E86"),sQuery(id+"F0.wireOp",EDGE,"E87"),sQuery(id+"F0.wireOp",EDGE,"E89"),sQuery(id+"F0.wireOp",EDGE,"E90"),sQuery(id+"F0.wireOp",EDGE,"E92"),sQuery(id+"F0.wireOp",EDGE,"E93"),sQuery(id+"F0.wireOp",EDGE,"E95"),sQuery(id+"F0.wireOp",EDGE,"E96"),sQuery(id+"F0.wireOp",EDGE,"E98"),sQuery(id+"F0.wireOp",EDGE,"E99")])]});
            hole(context, id + "F21", {"style" : HoleStyle.SIMPLE, "endStyle" : HoleEndStyle.THROUGH, "oppositeDirection" : true, "holeDiameter" : 2.54 * mm, "tappedDepth" : 12.7 * mm, "tapClearance" : 3, "locations" : qUnion([Q0]), "scope" : qUnion([Q1])});
        }
        {
            var Q0;
            Q0=sQuery(id+"F10.wireOp",VERTEX,"E108.center");
            var Q1;
            Q1=makeQuery(id+"F1.opExtrude","SWEPT_BODY",BODY,{"disambiguationData":[OSD([sQuery(id+"F0.wireOp",EDGE,"E0"),sQuery(id+"F0.wireOp",EDGE,"E1"),sQuery(id+"F0.wireOp",EDGE,"E2"),sQuery(id+"F0.wireOp",EDGE,"E3"),sQuery(id+"F0.wireOp",EDGE,"E4"),sQuery(id+"F0.wireOp",EDGE,"E5"),sQuery(id+"F0.wireOp",EDGE,"E6"),sQuery(id+"F0.wireOp",EDGE,"E7"),sQuery(id+"F0.wireOp",EDGE,"E8"),sQuery(id+"F0.wireOp",EDGE,"E9"),sQuery(id+"F0.wireOp",EDGE,"E10"),sQuery(id+"F0.wireOp",EDGE,"E11"),sQuery(id+"F0.wireOp",EDGE,"E12"),sQuery(id+"F0.wireOp",EDGE,"E13"),sQuery(id+"F0.wireOp",EDGE,"E14"),sQuery(id+"F0.wireOp",EDGE,"E15"),sQuery(id+"F0.wireOp",EDGE,"E16"),sQuery(id+"F0.wireOp",EDGE,"E17"),sQuery(id+"F0.wireOp",EDGE,"E18"),sQuery(id+"F0.wireOp",EDGE,"E19"),sQuery(id+"F0.wireOp",EDGE,"E20"),sQuery(id+"F0.wireOp",EDGE,"E21"),sQuery(id+"F0.wireOp",EDGE,"E22"),sQuery(id+"F0.wireOp",EDGE,"E23"),sQuery(id+"F0.wireOp",EDGE,"E24"),sQuery(id+"F0.wireOp",EDGE,"E25"),sQuery(id+"F0.wireOp",EDGE,"E26"),sQuery(id+"F0.wireOp",EDGE,"E27"),sQuery(id+"F0.wireOp",EDGE,"E28"),sQuery(id+"F0.wireOp",EDGE,"E29"),sQuery(id+"F0.wireOp",EDGE,"E30"),sQuery(id+"F0.wireOp",EDGE,"E31"),sQuery(id+"F0.wireOp",EDGE,"E32"),sQuery(id+"F0.wireOp",EDGE,"E33"),sQuery(id+"F0.wireOp",EDGE,"E34"),sQuery(id+"F0.wireOp",EDGE,"E35"),sQuery(id+"F0.wireOp",EDGE,"E36"),sQuery(id+"F0.wireOp",EDGE,"E37"),sQuery(id+"F0.wireOp",EDGE,"E38"),sQuery(id+"F0.wireOp",EDGE,"E39"),sQuery(id+"F0.wireOp",EDGE,"E40"),sQuery(id+"F0.wireOp",EDGE,"E41"),sQuery(id+"F0.wireOp",EDGE,"E42"),sQuery(id+"F0.wireOp",EDGE,"E43"),sQuery(id+"F0.wireOp",EDGE,"E44"),sQuery(id+"F0.wireOp",EDGE,"E45"),sQuery(id+"F0.wireOp",EDGE,"E46"),sQuery(id+"F0.wireOp",EDGE,"E47"),sQuery(id+"F0.wireOp",EDGE,"E48"),sQuery(id+"F0.wireOp",EDGE,"E49"),sQuery(id+"F0.wireOp",EDGE,"E50"),sQuery(id+"F0.wireOp",EDGE,"E51"),sQuery(id+"F0.wireOp",EDGE,"E52"),sQuery(id+"F0.wireOp",EDGE,"E53"),sQuery(id+"F0.wireOp",EDGE,"E54"),sQuery(id+"F0.wireOp",EDGE,"E55"),sQuery(id+"F0.wireOp",EDGE,"E56"),sQuery(id+"F0.wireOp",EDGE,"E57"),sQuery(id+"F0.wireOp",EDGE,"E58"),sQuery(id+"F0.wireOp",EDGE,"E59"),sQuery(id+"F0.wireOp",EDGE,"E60"),sQuery(id+"F0.wireOp",EDGE,"E61"),sQuery(id+"F0.wireOp",EDGE,"E62"),sQuery(id+"F0.wireOp",EDGE,"E63"),sQuery(id+"F0.wireOp",EDGE,"E64"),sQuery(id+"F0.wireOp",EDGE,"E65"),sQuery(id+"F0.wireOp",EDGE,"E66"),sQuery(id+"F0.wireOp",EDGE,"E67"),sQuery(id+"F0.wireOp",EDGE,"E68"),sQuery(id+"F0.wireOp",EDGE,"E69"),sQuery(id+"F0.wireOp",EDGE,"E70"),sQuery(id+"F0.wireOp",EDGE,"E71"),sQuery(id+"F0.wireOp",EDGE,"E72"),sQuery(id+"F0.wireOp",EDGE,"E73"),sQuery(id+"F0.wireOp",EDGE,"E74"),sQuery(id+"F0.wireOp",EDGE,"E75"),sQuery(id+"F0.wireOp",EDGE,"E76"),sQuery(id+"F0.wireOp",EDGE,"E77"),sQuery(id+"F0.wireOp",EDGE,"E78"),sQuery(id+"F0.wireOp",EDGE,"E79"),sQuery(id+"F0.wireOp",EDGE,"E80"),sQuery(id+"F0.wireOp",EDGE,"E81"),sQuery(id+"F0.wireOp",EDGE,"E82"),sQuery(id+"F0.wireOp",EDGE,"E83"),sQuery(id+"F0.wireOp",EDGE,"E84"),sQuery(id+"F0.wireOp",EDGE,"E85"),sQuery(id+"F0.wireOp",EDGE,"E86"),sQuery(id+"F0.wireOp",EDGE,"E87"),sQuery(id+"F0.wireOp",EDGE,"E89"),sQuery(id+"F0.wireOp",EDGE,"E90"),sQuery(id+"F0.wireOp",EDGE,"E92"),sQuery(id+"F0.wireOp",EDGE,"E93"),sQuery(id+"F0.wireOp",EDGE,"E95"),sQuery(id+"F0.wireOp",EDGE,"E96"),sQuery(id+"F0.wireOp",EDGE,"E98"),sQuery(id+"F0.wireOp",EDGE,"E99")])]});
            hole(context, id + "F22", {"style" : HoleStyle.SIMPLE, "endStyle" : HoleEndStyle.THROUGH, "oppositeDirection" : true, "holeDiameter" : 2.54 * mm, "tappedDepth" : 12.7 * mm, "tapClearance" : 3, "locations" : qUnion([Q0]), "scope" : qUnion([Q1])});
        }
        {
            var Q0;
            Q0=sQuery(id+"F11.wireOp",VERTEX,"E109.center");
            var Q1;
            Q1=makeQuery(id+"F1.opExtrude","SWEPT_BODY",BODY,{"disambiguationData":[OSD([sQuery(id+"F0.wireOp",EDGE,"E0"),sQuery(id+"F0.wireOp",EDGE,"E1"),sQuery(id+"F0.wireOp",EDGE,"E2"),sQuery(id+"F0.wireOp",EDGE,"E3"),sQuery(id+"F0.wireOp",EDGE,"E4"),sQuery(id+"F0.wireOp",EDGE,"E5"),sQuery(id+"F0.wireOp",EDGE,"E6"),sQuery(id+"F0.wireOp",EDGE,"E7"),sQuery(id+"F0.wireOp",EDGE,"E8"),sQuery(id+"F0.wireOp",EDGE,"E9"),sQuery(id+"F0.wireOp",EDGE,"E10"),sQuery(id+"F0.wireOp",EDGE,"E11"),sQuery(id+"F0.wireOp",EDGE,"E12"),sQuery(id+"F0.wireOp",EDGE,"E13"),sQuery(id+"F0.wireOp",EDGE,"E14"),sQuery(id+"F0.wireOp",EDGE,"E15"),sQuery(id+"F0.wireOp",EDGE,"E16"),sQuery(id+"F0.wireOp",EDGE,"E17"),sQuery(id+"F0.wireOp",EDGE,"E18"),sQuery(id+"F0.wireOp",EDGE,"E19"),sQuery(id+"F0.wireOp",EDGE,"E20"),sQuery(id+"F0.wireOp",EDGE,"E21"),sQuery(id+"F0.wireOp",EDGE,"E22"),sQuery(id+"F0.wireOp",EDGE,"E23"),sQuery(id+"F0.wireOp",EDGE,"E24"),sQuery(id+"F0.wireOp",EDGE,"E25"),sQuery(id+"F0.wireOp",EDGE,"E26"),sQuery(id+"F0.wireOp",EDGE,"E27"),sQuery(id+"F0.wireOp",EDGE,"E28"),sQuery(id+"F0.wireOp",EDGE,"E29"),sQuery(id+"F0.wireOp",EDGE,"E30"),sQuery(id+"F0.wireOp",EDGE,"E31"),sQuery(id+"F0.wireOp",EDGE,"E32"),sQuery(id+"F0.wireOp",EDGE,"E33"),sQuery(id+"F0.wireOp",EDGE,"E34"),sQuery(id+"F0.wireOp",EDGE,"E35"),sQuery(id+"F0.wireOp",EDGE,"E36"),sQuery(id+"F0.wireOp",EDGE,"E37"),sQuery(id+"F0.wireOp",EDGE,"E38"),sQuery(id+"F0.wireOp",EDGE,"E39"),sQuery(id+"F0.wireOp",EDGE,"E40"),sQuery(id+"F0.wireOp",EDGE,"E41"),sQuery(id+"F0.wireOp",EDGE,"E42"),sQuery(id+"F0.wireOp",EDGE,"E43"),sQuery(id+"F0.wireOp",EDGE,"E44"),sQuery(id+"F0.wireOp",EDGE,"E45"),sQuery(id+"F0.wireOp",EDGE,"E46"),sQuery(id+"F0.wireOp",EDGE,"E47"),sQuery(id+"F0.wireOp",EDGE,"E48"),sQuery(id+"F0.wireOp",EDGE,"E49"),sQuery(id+"F0.wireOp",EDGE,"E50"),sQuery(id+"F0.wireOp",EDGE,"E51"),sQuery(id+"F0.wireOp",EDGE,"E52"),sQuery(id+"F0.wireOp",EDGE,"E53"),sQuery(id+"F0.wireOp",EDGE,"E54"),sQuery(id+"F0.wireOp",EDGE,"E55"),sQuery(id+"F0.wireOp",EDGE,"E56"),sQuery(id+"F0.wireOp",EDGE,"E57"),sQuery(id+"F0.wireOp",EDGE,"E58"),sQuery(id+"F0.wireOp",EDGE,"E59"),sQuery(id+"F0.wireOp",EDGE,"E60"),sQuery(id+"F0.wireOp",EDGE,"E61"),sQuery(id+"F0.wireOp",EDGE,"E62"),sQuery(id+"F0.wireOp",EDGE,"E63"),sQuery(id+"F0.wireOp",EDGE,"E64"),sQuery(id+"F0.wireOp",EDGE,"E65"),sQuery(id+"F0.wireOp",EDGE,"E66"),sQuery(id+"F0.wireOp",EDGE,"E67"),sQuery(id+"F0.wireOp",EDGE,"E68"),sQuery(id+"F0.wireOp",EDGE,"E69"),sQuery(id+"F0.wireOp",EDGE,"E70"),sQuery(id+"F0.wireOp",EDGE,"E71"),sQuery(id+"F0.wireOp",EDGE,"E72"),sQuery(id+"F0.wireOp",EDGE,"E73"),sQuery(id+"F0.wireOp",EDGE,"E74"),sQuery(id+"F0.wireOp",EDGE,"E75"),sQuery(id+"F0.wireOp",EDGE,"E76"),sQuery(id+"F0.wireOp",EDGE,"E77"),sQuery(id+"F0.wireOp",EDGE,"E78"),sQuery(id+"F0.wireOp",EDGE,"E79"),sQuery(id+"F0.wireOp",EDGE,"E80"),sQuery(id+"F0.wireOp",EDGE,"E81"),sQuery(id+"F0.wireOp",EDGE,"E82"),sQuery(id+"F0.wireOp",EDGE,"E83"),sQuery(id+"F0.wireOp",EDGE,"E84"),sQuery(id+"F0.wireOp",EDGE,"E85"),sQuery(id+"F0.wireOp",EDGE,"E86"),sQuery(id+"F0.wireOp",EDGE,"E87"),sQuery(id+"F0.wireOp",EDGE,"E89"),sQuery(id+"F0.wireOp",EDGE,"E90"),sQuery(id+"F0.wireOp",EDGE,"E92"),sQuery(id+"F0.wireOp",EDGE,"E93"),sQuery(id+"F0.wireOp",EDGE,"E95"),sQuery(id+"F0.wireOp",EDGE,"E96"),sQuery(id+"F0.wireOp",EDGE,"E98"),sQuery(id+"F0.wireOp",EDGE,"E99")])]});
            hole(context, id + "F23", {"style" : HoleStyle.SIMPLE, "endStyle" : HoleEndStyle.THROUGH, "oppositeDirection" : true, "holeDiameter" : 2.54 * mm, "tappedDepth" : 12.7 * mm, "tapClearance" : 3, "locations" : qUnion([Q0]), "scope" : qUnion([Q1])});
        }
        {
            var Q0;
            Q0=sQuery(id+"F8.wireOp",VERTEX,"E106.center");
            var Q1;
            Q1=makeQuery(id+"F1.opExtrude","SWEPT_BODY",BODY,{"disambiguationData":[OSD([sQuery(id+"F0.wireOp",EDGE,"E0"),sQuery(id+"F0.wireOp",EDGE,"E1"),sQuery(id+"F0.wireOp",EDGE,"E2"),sQuery(id+"F0.wireOp",EDGE,"E3"),sQuery(id+"F0.wireOp",EDGE,"E4"),sQuery(id+"F0.wireOp",EDGE,"E5"),sQuery(id+"F0.wireOp",EDGE,"E6"),sQuery(id+"F0.wireOp",EDGE,"E7"),sQuery(id+"F0.wireOp",EDGE,"E8"),sQuery(id+"F0.wireOp",EDGE,"E9"),sQuery(id+"F0.wireOp",EDGE,"E10"),sQuery(id+"F0.wireOp",EDGE,"E11"),sQuery(id+"F0.wireOp",EDGE,"E12"),sQuery(id+"F0.wireOp",EDGE,"E13"),sQuery(id+"F0.wireOp",EDGE,"E14"),sQuery(id+"F0.wireOp",EDGE,"E15"),sQuery(id+"F0.wireOp",EDGE,"E16"),sQuery(id+"F0.wireOp",EDGE,"E17"),sQuery(id+"F0.wireOp",EDGE,"E18"),sQuery(id+"F0.wireOp",EDGE,"E19"),sQuery(id+"F0.wireOp",EDGE,"E20"),sQuery(id+"F0.wireOp",EDGE,"E21"),sQuery(id+"F0.wireOp",EDGE,"E22"),sQuery(id+"F0.wireOp",EDGE,"E23"),sQuery(id+"F0.wireOp",EDGE,"E24"),sQuery(id+"F0.wireOp",EDGE,"E25"),sQuery(id+"F0.wireOp",EDGE,"E26"),sQuery(id+"F0.wireOp",EDGE,"E27"),sQuery(id+"F0.wireOp",EDGE,"E28"),sQuery(id+"F0.wireOp",EDGE,"E29"),sQuery(id+"F0.wireOp",EDGE,"E30"),sQuery(id+"F0.wireOp",EDGE,"E31"),sQuery(id+"F0.wireOp",EDGE,"E32"),sQuery(id+"F0.wireOp",EDGE,"E33"),sQuery(id+"F0.wireOp",EDGE,"E34"),sQuery(id+"F0.wireOp",EDGE,"E35"),sQuery(id+"F0.wireOp",EDGE,"E36"),sQuery(id+"F0.wireOp",EDGE,"E37"),sQuery(id+"F0.wireOp",EDGE,"E38"),sQuery(id+"F0.wireOp",EDGE,"E39"),sQuery(id+"F0.wireOp",EDGE,"E40"),sQuery(id+"F0.wireOp",EDGE,"E41"),sQuery(id+"F0.wireOp",EDGE,"E42"),sQuery(id+"F0.wireOp",EDGE,"E43"),sQuery(id+"F0.wireOp",EDGE,"E44"),sQuery(id+"F0.wireOp",EDGE,"E45"),sQuery(id+"F0.wireOp",EDGE,"E46"),sQuery(id+"F0.wireOp",EDGE,"E47"),sQuery(id+"F0.wireOp",EDGE,"E48"),sQuery(id+"F0.wireOp",EDGE,"E49"),sQuery(id+"F0.wireOp",EDGE,"E50"),sQuery(id+"F0.wireOp",EDGE,"E51"),sQuery(id+"F0.wireOp",EDGE,"E52"),sQuery(id+"F0.wireOp",EDGE,"E53"),sQuery(id+"F0.wireOp",EDGE,"E54"),sQuery(id+"F0.wireOp",EDGE,"E55"),sQuery(id+"F0.wireOp",EDGE,"E56"),sQuery(id+"F0.wireOp",EDGE,"E57"),sQuery(id+"F0.wireOp",EDGE,"E58"),sQuery(id+"F0.wireOp",EDGE,"E59"),sQuery(id+"F0.wireOp",EDGE,"E60"),sQuery(id+"F0.wireOp",EDGE,"E61"),sQuery(id+"F0.wireOp",EDGE,"E62"),sQuery(id+"F0.wireOp",EDGE,"E63"),sQuery(id+"F0.wireOp",EDGE,"E64"),sQuery(id+"F0.wireOp",EDGE,"E65"),sQuery(id+"F0.wireOp",EDGE,"E66"),sQuery(id+"F0.wireOp",EDGE,"E67"),sQuery(id+"F0.wireOp",EDGE,"E68"),sQuery(id+"F0.wireOp",EDGE,"E69"),sQuery(id+"F0.wireOp",EDGE,"E70"),sQuery(id+"F0.wireOp",EDGE,"E71"),sQuery(id+"F0.wireOp",EDGE,"E72"),sQuery(id+"F0.wireOp",EDGE,"E73"),sQuery(id+"F0.wireOp",EDGE,"E74"),sQuery(id+"F0.wireOp",EDGE,"E75"),sQuery(id+"F0.wireOp",EDGE,"E76"),sQuery(id+"F0.wireOp",EDGE,"E77"),sQuery(id+"F0.wireOp",EDGE,"E78"),sQuery(id+"F0.wireOp",EDGE,"E79"),sQuery(id+"F0.wireOp",EDGE,"E80"),sQuery(id+"F0.wireOp",EDGE,"E81"),sQuery(id+"F0.wireOp",EDGE,"E82"),sQuery(id+"F0.wireOp",EDGE,"E83"),sQuery(id+"F0.wireOp",EDGE,"E84"),sQuery(id+"F0.wireOp",EDGE,"E85"),sQuery(id+"F0.wireOp",EDGE,"E86"),sQuery(id+"F0.wireOp",EDGE,"E87"),sQuery(id+"F0.wireOp",EDGE,"E89"),sQuery(id+"F0.wireOp",EDGE,"E90"),sQuery(id+"F0.wireOp",EDGE,"E92"),sQuery(id+"F0.wireOp",EDGE,"E93"),sQuery(id+"F0.wireOp",EDGE,"E95"),sQuery(id+"F0.wireOp",EDGE,"E96"),sQuery(id+"F0.wireOp",EDGE,"E98"),sQuery(id+"F0.wireOp",EDGE,"E99")])]});
            hole(context, id + "F24", {"style" : HoleStyle.SIMPLE, "endStyle" : HoleEndStyle.THROUGH, "oppositeDirection" : true, "holeDiameter" : 2.54 * mm, "tappedDepth" : 12.7 * mm, "tapClearance" : 3, "locations" : qUnion([Q0]), "scope" : qUnion([Q1])});
        }
        {
            var Q0;
            Q0=sQuery(id+"F9.wireOp",VERTEX,"E107.center");
            var Q1;
            Q1=makeQuery(id+"F1.opExtrude","SWEPT_BODY",BODY,{"disambiguationData":[OSD([sQuery(id+"F0.wireOp",EDGE,"E0"),sQuery(id+"F0.wireOp",EDGE,"E1"),sQuery(id+"F0.wireOp",EDGE,"E2"),sQuery(id+"F0.wireOp",EDGE,"E3"),sQuery(id+"F0.wireOp",EDGE,"E4"),sQuery(id+"F0.wireOp",EDGE,"E5"),sQuery(id+"F0.wireOp",EDGE,"E6"),sQuery(id+"F0.wireOp",EDGE,"E7"),sQuery(id+"F0.wireOp",EDGE,"E8"),sQuery(id+"F0.wireOp",EDGE,"E9"),sQuery(id+"F0.wireOp",EDGE,"E10"),sQuery(id+"F0.wireOp",EDGE,"E11"),sQuery(id+"F0.wireOp",EDGE,"E12"),sQuery(id+"F0.wireOp",EDGE,"E13"),sQuery(id+"F0.wireOp",EDGE,"E14"),sQuery(id+"F0.wireOp",EDGE,"E15"),sQuery(id+"F0.wireOp",EDGE,"E16"),sQuery(id+"F0.wireOp",EDGE,"E17"),sQuery(id+"F0.wireOp",EDGE,"E18"),sQuery(id+"F0.wireOp",EDGE,"E19"),sQuery(id+"F0.wireOp",EDGE,"E20"),sQuery(id+"F0.wireOp",EDGE,"E21"),sQuery(id+"F0.wireOp",EDGE,"E22"),sQuery(id+"F0.wireOp",EDGE,"E23"),sQuery(id+"F0.wireOp",EDGE,"E24"),sQuery(id+"F0.wireOp",EDGE,"E25"),sQuery(id+"F0.wireOp",EDGE,"E26"),sQuery(id+"F0.wireOp",EDGE,"E27"),sQuery(id+"F0.wireOp",EDGE,"E28"),sQuery(id+"F0.wireOp",EDGE,"E29"),sQuery(id+"F0.wireOp",EDGE,"E30"),sQuery(id+"F0.wireOp",EDGE,"E31"),sQuery(id+"F0.wireOp",EDGE,"E32"),sQuery(id+"F0.wireOp",EDGE,"E33"),sQuery(id+"F0.wireOp",EDGE,"E34"),sQuery(id+"F0.wireOp",EDGE,"E35"),sQuery(id+"F0.wireOp",EDGE,"E36"),sQuery(id+"F0.wireOp",EDGE,"E37"),sQuery(id+"F0.wireOp",EDGE,"E38"),sQuery(id+"F0.wireOp",EDGE,"E39"),sQuery(id+"F0.wireOp",EDGE,"E40"),sQuery(id+"F0.wireOp",EDGE,"E41"),sQuery(id+"F0.wireOp",EDGE,"E42"),sQuery(id+"F0.wireOp",EDGE,"E43"),sQuery(id+"F0.wireOp",EDGE,"E44"),sQuery(id+"F0.wireOp",EDGE,"E45"),sQuery(id+"F0.wireOp",EDGE,"E46"),sQuery(id+"F0.wireOp",EDGE,"E47"),sQuery(id+"F0.wireOp",EDGE,"E48"),sQuery(id+"F0.wireOp",EDGE,"E49"),sQuery(id+"F0.wireOp",EDGE,"E50"),sQuery(id+"F0.wireOp",EDGE,"E51"),sQuery(id+"F0.wireOp",EDGE,"E52"),sQuery(id+"F0.wireOp",EDGE,"E53"),sQuery(id+"F0.wireOp",EDGE,"E54"),sQuery(id+"F0.wireOp",EDGE,"E55"),sQuery(id+"F0.wireOp",EDGE,"E56"),sQuery(id+"F0.wireOp",EDGE,"E57"),sQuery(id+"F0.wireOp",EDGE,"E58"),sQuery(id+"F0.wireOp",EDGE,"E59"),sQuery(id+"F0.wireOp",EDGE,"E60"),sQuery(id+"F0.wireOp",EDGE,"E61"),sQuery(id+"F0.wireOp",EDGE,"E62"),sQuery(id+"F0.wireOp",EDGE,"E63"),sQuery(id+"F0.wireOp",EDGE,"E64"),sQuery(id+"F0.wireOp",EDGE,"E65"),sQuery(id+"F0.wireOp",EDGE,"E66"),sQuery(id+"F0.wireOp",EDGE,"E67"),sQuery(id+"F0.wireOp",EDGE,"E68"),sQuery(id+"F0.wireOp",EDGE,"E69"),sQuery(id+"F0.wireOp",EDGE,"E70"),sQuery(id+"F0.wireOp",EDGE,"E71"),sQuery(id+"F0.wireOp",EDGE,"E72"),sQuery(id+"F0.wireOp",EDGE,"E73"),sQuery(id+"F0.wireOp",EDGE,"E74"),sQuery(id+"F0.wireOp",EDGE,"E75"),sQuery(id+"F0.wireOp",EDGE,"E76"),sQuery(id+"F0.wireOp",EDGE,"E77"),sQuery(id+"F0.wireOp",EDGE,"E78"),sQuery(id+"F0.wireOp",EDGE,"E79"),sQuery(id+"F0.wireOp",EDGE,"E80"),sQuery(id+"F0.wireOp",EDGE,"E81"),sQuery(id+"F0.wireOp",EDGE,"E82"),sQuery(id+"F0.wireOp",EDGE,"E83"),sQuery(id+"F0.wireOp",EDGE,"E84"),sQuery(id+"F0.wireOp",EDGE,"E85"),sQuery(id+"F0.wireOp",EDGE,"E86"),sQuery(id+"F0.wireOp",EDGE,"E87"),sQuery(id+"F0.wireOp",EDGE,"E89"),sQuery(id+"F0.wireOp",EDGE,"E90"),sQuery(id+"F0.wireOp",EDGE,"E92"),sQuery(id+"F0.wireOp",EDGE,"E93"),sQuery(id+"F0.wireOp",EDGE,"E95"),sQuery(id+"F0.wireOp",EDGE,"E96"),sQuery(id+"F0.wireOp",EDGE,"E98"),sQuery(id+"F0.wireOp",EDGE,"E99")])]});
            hole(context, id + "F25", {"style" : HoleStyle.SIMPLE, "endStyle" : HoleEndStyle.THROUGH, "oppositeDirection" : true, "holeDiameter" : 2.54 * mm, "tappedDepth" : 12.7 * mm, "tapClearance" : 3, "locations" : qUnion([Q0]), "scope" : qUnion([Q1])});
        }
        {
            var Q0;
            Q0=sQuery(id+"F6.wireOp",VERTEX,"E104.center");
            var Q1;
            Q1=makeQuery(id+"F1.opExtrude","SWEPT_BODY",BODY,{"disambiguationData":[OSD([sQuery(id+"F0.wireOp",EDGE,"E0"),sQuery(id+"F0.wireOp",EDGE,"E1"),sQuery(id+"F0.wireOp",EDGE,"E2"),sQuery(id+"F0.wireOp",EDGE,"E3"),sQuery(id+"F0.wireOp",EDGE,"E4"),sQuery(id+"F0.wireOp",EDGE,"E5"),sQuery(id+"F0.wireOp",EDGE,"E6"),sQuery(id+"F0.wireOp",EDGE,"E7"),sQuery(id+"F0.wireOp",EDGE,"E8"),sQuery(id+"F0.wireOp",EDGE,"E9"),sQuery(id+"F0.wireOp",EDGE,"E10"),sQuery(id+"F0.wireOp",EDGE,"E11"),sQuery(id+"F0.wireOp",EDGE,"E12"),sQuery(id+"F0.wireOp",EDGE,"E13"),sQuery(id+"F0.wireOp",EDGE,"E14"),sQuery(id+"F0.wireOp",EDGE,"E15"),sQuery(id+"F0.wireOp",EDGE,"E16"),sQuery(id+"F0.wireOp",EDGE,"E17"),sQuery(id+"F0.wireOp",EDGE,"E18"),sQuery(id+"F0.wireOp",EDGE,"E19"),sQuery(id+"F0.wireOp",EDGE,"E20"),sQuery(id+"F0.wireOp",EDGE,"E21"),sQuery(id+"F0.wireOp",EDGE,"E22"),sQuery(id+"F0.wireOp",EDGE,"E23"),sQuery(id+"F0.wireOp",EDGE,"E24"),sQuery(id+"F0.wireOp",EDGE,"E25"),sQuery(id+"F0.wireOp",EDGE,"E26"),sQuery(id+"F0.wireOp",EDGE,"E27"),sQuery(id+"F0.wireOp",EDGE,"E28"),sQuery(id+"F0.wireOp",EDGE,"E29"),sQuery(id+"F0.wireOp",EDGE,"E30"),sQuery(id+"F0.wireOp",EDGE,"E31"),sQuery(id+"F0.wireOp",EDGE,"E32"),sQuery(id+"F0.wireOp",EDGE,"E33"),sQuery(id+"F0.wireOp",EDGE,"E34"),sQuery(id+"F0.wireOp",EDGE,"E35"),sQuery(id+"F0.wireOp",EDGE,"E36"),sQuery(id+"F0.wireOp",EDGE,"E37"),sQuery(id+"F0.wireOp",EDGE,"E38"),sQuery(id+"F0.wireOp",EDGE,"E39"),sQuery(id+"F0.wireOp",EDGE,"E40"),sQuery(id+"F0.wireOp",EDGE,"E41"),sQuery(id+"F0.wireOp",EDGE,"E42"),sQuery(id+"F0.wireOp",EDGE,"E43"),sQuery(id+"F0.wireOp",EDGE,"E44"),sQuery(id+"F0.wireOp",EDGE,"E45"),sQuery(id+"F0.wireOp",EDGE,"E46"),sQuery(id+"F0.wireOp",EDGE,"E47"),sQuery(id+"F0.wireOp",EDGE,"E48"),sQuery(id+"F0.wireOp",EDGE,"E49"),sQuery(id+"F0.wireOp",EDGE,"E50"),sQuery(id+"F0.wireOp",EDGE,"E51"),sQuery(id+"F0.wireOp",EDGE,"E52"),sQuery(id+"F0.wireOp",EDGE,"E53"),sQuery(id+"F0.wireOp",EDGE,"E54"),sQuery(id+"F0.wireOp",EDGE,"E55"),sQuery(id+"F0.wireOp",EDGE,"E56"),sQuery(id+"F0.wireOp",EDGE,"E57"),sQuery(id+"F0.wireOp",EDGE,"E58"),sQuery(id+"F0.wireOp",EDGE,"E59"),sQuery(id+"F0.wireOp",EDGE,"E60"),sQuery(id+"F0.wireOp",EDGE,"E61"),sQuery(id+"F0.wireOp",EDGE,"E62"),sQuery(id+"F0.wireOp",EDGE,"E63"),sQuery(id+"F0.wireOp",EDGE,"E64"),sQuery(id+"F0.wireOp",EDGE,"E65"),sQuery(id+"F0.wireOp",EDGE,"E66"),sQuery(id+"F0.wireOp",EDGE,"E67"),sQuery(id+"F0.wireOp",EDGE,"E68"),sQuery(id+"F0.wireOp",EDGE,"E69"),sQuery(id+"F0.wireOp",EDGE,"E70"),sQuery(id+"F0.wireOp",EDGE,"E71"),sQuery(id+"F0.wireOp",EDGE,"E72"),sQuery(id+"F0.wireOp",EDGE,"E73"),sQuery(id+"F0.wireOp",EDGE,"E74"),sQuery(id+"F0.wireOp",EDGE,"E75"),sQuery(id+"F0.wireOp",EDGE,"E76"),sQuery(id+"F0.wireOp",EDGE,"E77"),sQuery(id+"F0.wireOp",EDGE,"E78"),sQuery(id+"F0.wireOp",EDGE,"E79"),sQuery(id+"F0.wireOp",EDGE,"E80"),sQuery(id+"F0.wireOp",EDGE,"E81"),sQuery(id+"F0.wireOp",EDGE,"E82"),sQuery(id+"F0.wireOp",EDGE,"E83"),sQuery(id+"F0.wireOp",EDGE,"E84"),sQuery(id+"F0.wireOp",EDGE,"E85"),sQuery(id+"F0.wireOp",EDGE,"E86"),sQuery(id+"F0.wireOp",EDGE,"E87"),sQuery(id+"F0.wireOp",EDGE,"E89"),sQuery(id+"F0.wireOp",EDGE,"E90"),sQuery(id+"F0.wireOp",EDGE,"E92"),sQuery(id+"F0.wireOp",EDGE,"E93"),sQuery(id+"F0.wireOp",EDGE,"E95"),sQuery(id+"F0.wireOp",EDGE,"E96"),sQuery(id+"F0.wireOp",EDGE,"E98"),sQuery(id+"F0.wireOp",EDGE,"E99")])]});
            hole(context, id + "F26", {"style" : HoleStyle.SIMPLE, "endStyle" : HoleEndStyle.THROUGH, "oppositeDirection" : true, "holeDiameter" : 2.54 * mm, "tappedDepth" : 12.7 * mm, "tapClearance" : 3, "locations" : qUnion([Q0]), "scope" : qUnion([Q1])});
        }
        {
            var Q0;
            Q0=sQuery(id+"F7.wireOp",VERTEX,"E105.center");
            var Q1;
            Q1=makeQuery(id+"F1.opExtrude","SWEPT_BODY",BODY,{"disambiguationData":[OSD([sQuery(id+"F0.wireOp",EDGE,"E0"),sQuery(id+"F0.wireOp",EDGE,"E1"),sQuery(id+"F0.wireOp",EDGE,"E2"),sQuery(id+"F0.wireOp",EDGE,"E3"),sQuery(id+"F0.wireOp",EDGE,"E4"),sQuery(id+"F0.wireOp",EDGE,"E5"),sQuery(id+"F0.wireOp",EDGE,"E6"),sQuery(id+"F0.wireOp",EDGE,"E7"),sQuery(id+"F0.wireOp",EDGE,"E8"),sQuery(id+"F0.wireOp",EDGE,"E9"),sQuery(id+"F0.wireOp",EDGE,"E10"),sQuery(id+"F0.wireOp",EDGE,"E11"),sQuery(id+"F0.wireOp",EDGE,"E12"),sQuery(id+"F0.wireOp",EDGE,"E13"),sQuery(id+"F0.wireOp",EDGE,"E14"),sQuery(id+"F0.wireOp",EDGE,"E15"),sQuery(id+"F0.wireOp",EDGE,"E16"),sQuery(id+"F0.wireOp",EDGE,"E17"),sQuery(id+"F0.wireOp",EDGE,"E18"),sQuery(id+"F0.wireOp",EDGE,"E19"),sQuery(id+"F0.wireOp",EDGE,"E20"),sQuery(id+"F0.wireOp",EDGE,"E21"),sQuery(id+"F0.wireOp",EDGE,"E22"),sQuery(id+"F0.wireOp",EDGE,"E23"),sQuery(id+"F0.wireOp",EDGE,"E24"),sQuery(id+"F0.wireOp",EDGE,"E25"),sQuery(id+"F0.wireOp",EDGE,"E26"),sQuery(id+"F0.wireOp",EDGE,"E27"),sQuery(id+"F0.wireOp",EDGE,"E28"),sQuery(id+"F0.wireOp",EDGE,"E29"),sQuery(id+"F0.wireOp",EDGE,"E30"),sQuery(id+"F0.wireOp",EDGE,"E31"),sQuery(id+"F0.wireOp",EDGE,"E32"),sQuery(id+"F0.wireOp",EDGE,"E33"),sQuery(id+"F0.wireOp",EDGE,"E34"),sQuery(id+"F0.wireOp",EDGE,"E35"),sQuery(id+"F0.wireOp",EDGE,"E36"),sQuery(id+"F0.wireOp",EDGE,"E37"),sQuery(id+"F0.wireOp",EDGE,"E38"),sQuery(id+"F0.wireOp",EDGE,"E39"),sQuery(id+"F0.wireOp",EDGE,"E40"),sQuery(id+"F0.wireOp",EDGE,"E41"),sQuery(id+"F0.wireOp",EDGE,"E42"),sQuery(id+"F0.wireOp",EDGE,"E43"),sQuery(id+"F0.wireOp",EDGE,"E44"),sQuery(id+"F0.wireOp",EDGE,"E45"),sQuery(id+"F0.wireOp",EDGE,"E46"),sQuery(id+"F0.wireOp",EDGE,"E47"),sQuery(id+"F0.wireOp",EDGE,"E48"),sQuery(id+"F0.wireOp",EDGE,"E49"),sQuery(id+"F0.wireOp",EDGE,"E50"),sQuery(id+"F0.wireOp",EDGE,"E51"),sQuery(id+"F0.wireOp",EDGE,"E52"),sQuery(id+"F0.wireOp",EDGE,"E53"),sQuery(id+"F0.wireOp",EDGE,"E54"),sQuery(id+"F0.wireOp",EDGE,"E55"),sQuery(id+"F0.wireOp",EDGE,"E56"),sQuery(id+"F0.wireOp",EDGE,"E57"),sQuery(id+"F0.wireOp",EDGE,"E58"),sQuery(id+"F0.wireOp",EDGE,"E59"),sQuery(id+"F0.wireOp",EDGE,"E60"),sQuery(id+"F0.wireOp",EDGE,"E61"),sQuery(id+"F0.wireOp",EDGE,"E62"),sQuery(id+"F0.wireOp",EDGE,"E63"),sQuery(id+"F0.wireOp",EDGE,"E64"),sQuery(id+"F0.wireOp",EDGE,"E65"),sQuery(id+"F0.wireOp",EDGE,"E66"),sQuery(id+"F0.wireOp",EDGE,"E67"),sQuery(id+"F0.wireOp",EDGE,"E68"),sQuery(id+"F0.wireOp",EDGE,"E69"),sQuery(id+"F0.wireOp",EDGE,"E70"),sQuery(id+"F0.wireOp",EDGE,"E71"),sQuery(id+"F0.wireOp",EDGE,"E72"),sQuery(id+"F0.wireOp",EDGE,"E73"),sQuery(id+"F0.wireOp",EDGE,"E74"),sQuery(id+"F0.wireOp",EDGE,"E75"),sQuery(id+"F0.wireOp",EDGE,"E76"),sQuery(id+"F0.wireOp",EDGE,"E77"),sQuery(id+"F0.wireOp",EDGE,"E78"),sQuery(id+"F0.wireOp",EDGE,"E79"),sQuery(id+"F0.wireOp",EDGE,"E80"),sQuery(id+"F0.wireOp",EDGE,"E81"),sQuery(id+"F0.wireOp",EDGE,"E82"),sQuery(id+"F0.wireOp",EDGE,"E83"),sQuery(id+"F0.wireOp",EDGE,"E84"),sQuery(id+"F0.wireOp",EDGE,"E85"),sQuery(id+"F0.wireOp",EDGE,"E86"),sQuery(id+"F0.wireOp",EDGE,"E87"),sQuery(id+"F0.wireOp",EDGE,"E89"),sQuery(id+"F0.wireOp",EDGE,"E90"),sQuery(id+"F0.wireOp",EDGE,"E92"),sQuery(id+"F0.wireOp",EDGE,"E93"),sQuery(id+"F0.wireOp",EDGE,"E95"),sQuery(id+"F0.wireOp",EDGE,"E96"),sQuery(id+"F0.wireOp",EDGE,"E98"),sQuery(id+"F0.wireOp",EDGE,"E99")])]});
            hole(context, id + "F27", {"style" : HoleStyle.SIMPLE, "endStyle" : HoleEndStyle.THROUGH, "oppositeDirection" : true, "holeDiameter" : 2.54 * mm, "tappedDepth" : 12.7 * mm, "tapClearance" : 3, "locations" : qUnion([Q0]), "scope" : qUnion([Q1])});
        }
    });
